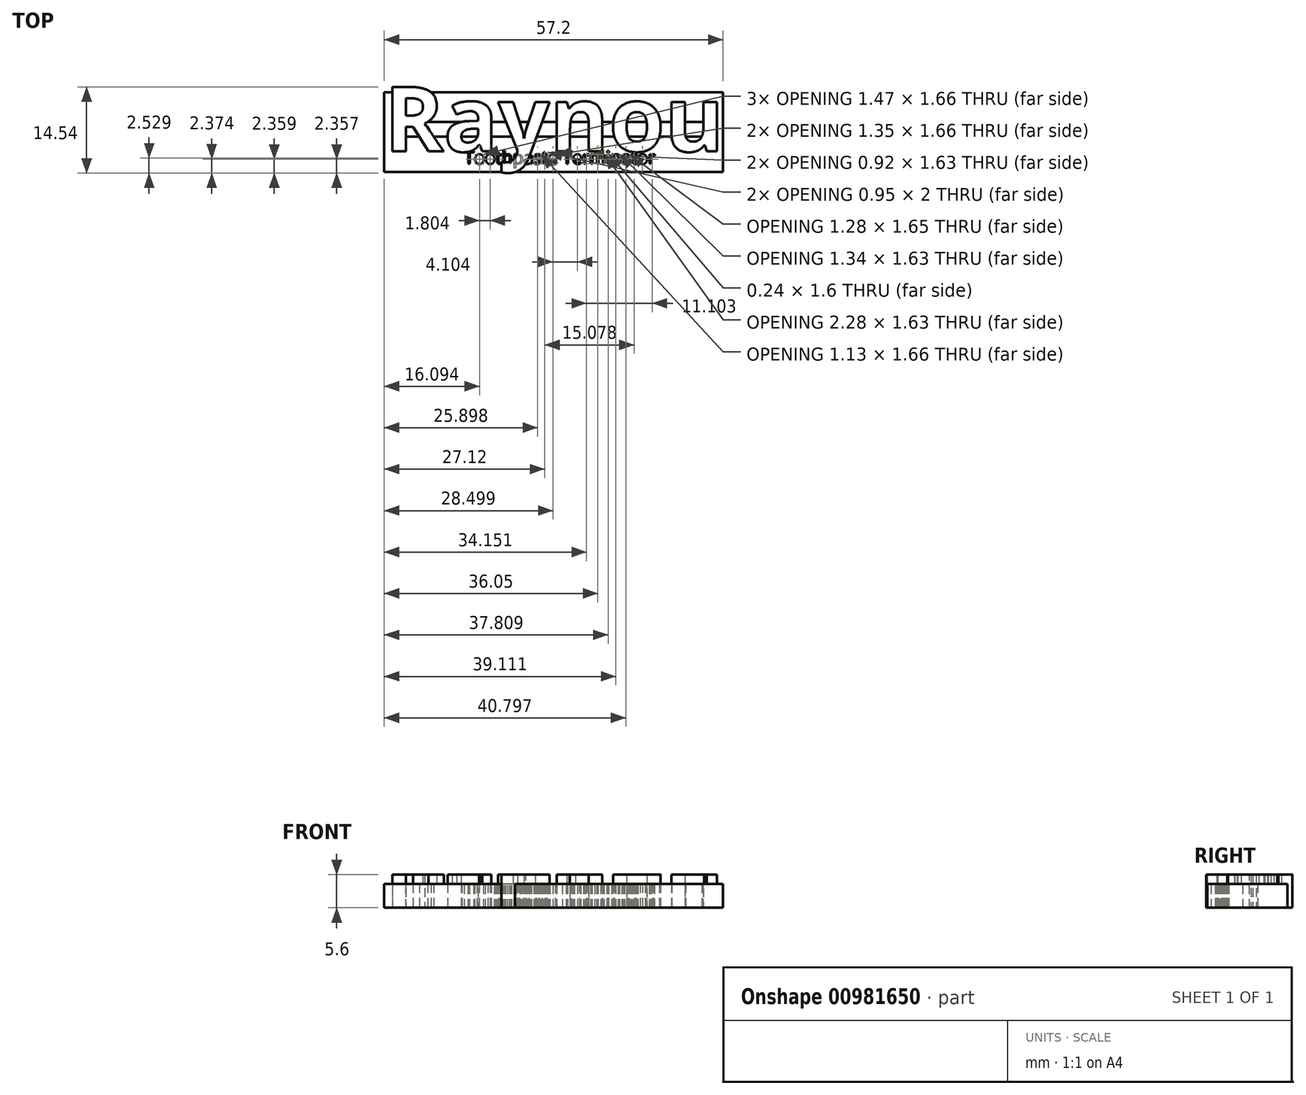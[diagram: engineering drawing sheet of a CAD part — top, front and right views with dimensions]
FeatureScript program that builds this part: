
annotation { "Feature Type Name" : "Feature", "Feature Type Description" : "" }
export const myFeature = defineFeature(function(context is Context, id is Id, definition is map)
    precondition{}
    {
        {
            var Q0;
            Q0=qCreatedBy(makeId("Top.planeOp"),FACE);
            var sketch = newSketch(context, id + "F0", { "sketchPlane" : qUnion([Q0])});
            skLineSegment(sketch, "E0.bottom", {"start": v(-0.37, 8.9) * mm, "end": v(52.83, 8.9) * mm});
            skLineSegment(sketch, "E0.top", {"start": v(-0.37, 6.4) * mm, "end": v(52.83, 6.4) * mm});
            skLineSegment(sketch, "E0.left", {"start": v(-0.37, 8.9) * mm, "end": v(-0.37, 6.4) * mm});
            skLineSegment(sketch, "E0.right", {"start": v(52.83, 8.9) * mm, "end": v(52.83, 6.4) * mm});
            skLineSegment(sketch, "E1.0", {"start": v(-2.37, 13.9) * mm, "end": v(54.83, 13.9) * mm});
            skLineSegment(sketch, "E1.1", {"start": v(-2.37, 13.9) * mm, "end": v(-2.37, 0.4) * mm});
            skLineSegment(sketch, "E1.2", {"start": v(-2.37, 0.4) * mm, "end": v(54.83, 0.4) * mm});
            skLineSegment(sketch, "E1.3", {"start": v(54.83, 13.9) * mm, "end": v(54.83, 0.4) * mm});
            skSolve(sketch);
        }
        {
            var Q0;
            Q0=qCreatedBy(makeId("Top.planeOp"),FACE);
            var sketch = newSketch(context, id + "F1", { "sketchPlane" : qUnion([Q0])});
            skText(sketch, "E2", { "text": "Raynou", "fontName": "OpenSans-Bold.ttf"});
            const initialGuessF1  = {"E2": [-0.00237, 0.0039, 1, 0, 0.01097]};
            skSetInitialGuess(sketch, initialGuessF1);
            skSolve(sketch);
        }
        {
            var Q0;
            Q0=makeQuery(id+"F0.imprint","IMPRINT",FACE,{"disambiguationData":[TD([[makeQuery(id+"F0.imprint","IMPRINT",EDGE,{"derivedFrom":sQuery(id+"F0.wireOp",EDGE,"E0.bottom")}),1.0]])]});
            var Q1;
            Q1=makeQuery(id+"F1.imprint","IMPRINT",FACE,{"disambiguationData":[TD([[makeQuery(id+"F1.imprint","IMPRINT",EDGE,{"derivedFrom":sQuery(id+"F1.wireOp",EDGE,"E2.sketch_text.stroke-19")}),-1.0]])]});
            var Q2;
            Q2=makeQuery(id+"F1.imprint","IMPRINT",FACE,{"disambiguationData":[TD([[makeQuery(id+"F1.imprint","IMPRINT",EDGE,{"derivedFrom":sQuery(id+"F1.wireOp",EDGE,"E2.sketch_text.stroke-0")}),-1.0]])]});
            var Q3;
            Q3=makeQuery(id+"F1.imprint","IMPRINT",FACE,{"disambiguationData":[TD([[makeQuery(id+"F1.imprint","IMPRINT",EDGE,{"derivedFrom":sQuery(id+"F1.wireOp",EDGE,"E2.sketch_text.stroke-44")}),-1.0]])]});
            var Q4;
            Q4=makeQuery(id+"F1.imprint","IMPRINT",FACE,{"disambiguationData":[TD([[makeQuery(id+"F1.imprint","IMPRINT",EDGE,{"derivedFrom":sQuery(id+"F1.wireOp",EDGE,"E2.sketch_text.stroke-61")}),-1.0]])]});
            var Q5;
            Q5=makeQuery(id+"F1.imprint","IMPRINT",FACE,{"disambiguationData":[TD([[makeQuery(id+"F1.imprint","IMPRINT",EDGE,{"derivedFrom":sQuery(id+"F1.wireOp",EDGE,"E2.sketch_text.stroke-78")}),-1.0]])]});
            var Q6;
            Q6=makeQuery(id+"F1.imprint","IMPRINT",FACE,{"disambiguationData":[TD([[makeQuery(id+"F1.imprint","IMPRINT",EDGE,{"derivedFrom":sQuery(id+"F1.wireOp",EDGE,"E2.sketch_text.stroke-96")}),-1.0]])]});
            extrude(context, id + "F2", {"entities" : qUnion([Q0, Q1, Q2, Q3, Q4, Q5, Q6]), "depth" : 4 * mm, "offsetDistance" : 25 * mm});
        }
        {
            var Q0;
            Q0=makeQuery(id+"F2.opExtrude","SWEPT_BODY",BODY,{"disambiguationData":[OSD([sQuery(id+"F1.wireOp",EDGE,"E2.sketch_text.stroke-0"),sQuery(id+"F1.wireOp",EDGE,"E2.sketch_text.stroke-1"),sQuery(id+"F1.wireOp",EDGE,"E2.sketch_text.stroke-2"),sQuery(id+"F1.wireOp",EDGE,"E2.sketch_text.stroke-3"),sQuery(id+"F1.wireOp",EDGE,"E2.sketch_text.stroke-4"),sQuery(id+"F1.wireOp",EDGE,"E2.sketch_text.stroke-5"),sQuery(id+"F1.wireOp",EDGE,"E2.sketch_text.stroke-6"),sQuery(id+"F1.wireOp",EDGE,"E2.sketch_text.stroke-7"),sQuery(id+"F1.wireOp",EDGE,"E2.sketch_text.stroke-8"),sQuery(id+"F1.wireOp",EDGE,"E2.sketch_text.stroke-9"),sQuery(id+"F1.wireOp",EDGE,"E2.sketch_text.stroke-10"),sQuery(id+"F1.wireOp",EDGE,"E2.sketch_text.stroke-11"),sQuery(id+"F1.wireOp",EDGE,"E2.sketch_text.stroke-12"),sQuery(id+"F1.wireOp",EDGE,"E2.sketch_text.stroke-13"),sQuery(id+"F1.wireOp",EDGE,"E2.sketch_text.stroke-14"),sQuery(id+"F1.wireOp",EDGE,"E2.sketch_text.stroke-15"),sQuery(id+"F1.wireOp",EDGE,"E2.sketch_text.stroke-16"),sQuery(id+"F1.wireOp",EDGE,"E2.sketch_text.stroke-17"),sQuery(id+"F1.wireOp",EDGE,"E2.sketch_text.stroke-18")])]});
            var Q1;
            Q1=makeQuery(id+"F2.opExtrude","SWEPT_BODY",BODY,{"disambiguationData":[OSD([sQuery(id+"F0.wireOp",EDGE,"E0.bottom"),sQuery(id+"F0.wireOp",EDGE,"E0.top"),sQuery(id+"F0.wireOp",EDGE,"E0.left"),sQuery(id+"F0.wireOp",EDGE,"E0.right"),sQuery(id+"F0.wireOp",EDGE,"E1.0"),sQuery(id+"F0.wireOp",EDGE,"E1.1"),sQuery(id+"F0.wireOp",EDGE,"E1.2"),sQuery(id+"F0.wireOp",EDGE,"E1.3")])]});
            var Q2;
            Q2=makeQuery(id+"F2.opExtrude","SWEPT_BODY",BODY,{"disambiguationData":[OSD([sQuery(id+"F1.wireOp",EDGE,"E2.sketch_text.stroke-19"),sQuery(id+"F1.wireOp",EDGE,"E2.sketch_text.stroke-20"),sQuery(id+"F1.wireOp",EDGE,"E2.sketch_text.stroke-21"),sQuery(id+"F1.wireOp",EDGE,"E2.sketch_text.stroke-22"),sQuery(id+"F1.wireOp",EDGE,"E2.sketch_text.stroke-23"),sQuery(id+"F1.wireOp",EDGE,"E2.sketch_text.stroke-24"),sQuery(id+"F1.wireOp",EDGE,"E2.sketch_text.stroke-25"),sQuery(id+"F1.wireOp",EDGE,"E2.sketch_text.stroke-26"),sQuery(id+"F1.wireOp",EDGE,"E2.sketch_text.stroke-27"),sQuery(id+"F1.wireOp",EDGE,"E2.sketch_text.stroke-28"),sQuery(id+"F1.wireOp",EDGE,"E2.sketch_text.stroke-29"),sQuery(id+"F1.wireOp",EDGE,"E2.sketch_text.stroke-30"),sQuery(id+"F1.wireOp",EDGE,"E2.sketch_text.stroke-31"),sQuery(id+"F1.wireOp",EDGE,"E2.sketch_text.stroke-32"),sQuery(id+"F1.wireOp",EDGE,"E2.sketch_text.stroke-33"),sQuery(id+"F1.wireOp",EDGE,"E2.sketch_text.stroke-34"),sQuery(id+"F1.wireOp",EDGE,"E2.sketch_text.stroke-35"),sQuery(id+"F1.wireOp",EDGE,"E2.sketch_text.stroke-36"),sQuery(id+"F1.wireOp",EDGE,"E2.sketch_text.stroke-37"),sQuery(id+"F1.wireOp",EDGE,"E2.sketch_text.stroke-38"),sQuery(id+"F1.wireOp",EDGE,"E2.sketch_text.stroke-39"),sQuery(id+"F1.wireOp",EDGE,"E2.sketch_text.stroke-40"),sQuery(id+"F1.wireOp",EDGE,"E2.sketch_text.stroke-41"),sQuery(id+"F1.wireOp",EDGE,"E2.sketch_text.stroke-42"),sQuery(id+"F1.wireOp",EDGE,"E2.sketch_text.stroke-43")])]});
            var Q3;
            Q3=makeQuery(id+"F2.opExtrude","SWEPT_BODY",BODY,{"disambiguationData":[OSD([sQuery(id+"F1.wireOp",EDGE,"E2.sketch_text.stroke-44"),sQuery(id+"F1.wireOp",EDGE,"E2.sketch_text.stroke-45"),sQuery(id+"F1.wireOp",EDGE,"E2.sketch_text.stroke-46"),sQuery(id+"F1.wireOp",EDGE,"E2.sketch_text.stroke-47"),sQuery(id+"F1.wireOp",EDGE,"E2.sketch_text.stroke-48"),sQuery(id+"F1.wireOp",EDGE,"E2.sketch_text.stroke-49"),sQuery(id+"F1.wireOp",EDGE,"E2.sketch_text.stroke-50"),sQuery(id+"F1.wireOp",EDGE,"E2.sketch_text.stroke-51"),sQuery(id+"F1.wireOp",EDGE,"E2.sketch_text.stroke-52"),sQuery(id+"F1.wireOp",EDGE,"E2.sketch_text.stroke-53"),sQuery(id+"F1.wireOp",EDGE,"E2.sketch_text.stroke-54"),sQuery(id+"F1.wireOp",EDGE,"E2.sketch_text.stroke-55"),sQuery(id+"F1.wireOp",EDGE,"E2.sketch_text.stroke-56"),sQuery(id+"F1.wireOp",EDGE,"E2.sketch_text.stroke-57"),sQuery(id+"F1.wireOp",EDGE,"E2.sketch_text.stroke-58"),sQuery(id+"F1.wireOp",EDGE,"E2.sketch_text.stroke-59"),sQuery(id+"F1.wireOp",EDGE,"E2.sketch_text.stroke-60")])]});
            var Q4;
            Q4=makeQuery(id+"F2.opExtrude","SWEPT_BODY",BODY,{"disambiguationData":[OSD([sQuery(id+"F1.wireOp",EDGE,"E2.sketch_text.stroke-61"),sQuery(id+"F1.wireOp",EDGE,"E2.sketch_text.stroke-62"),sQuery(id+"F1.wireOp",EDGE,"E2.sketch_text.stroke-63"),sQuery(id+"F1.wireOp",EDGE,"E2.sketch_text.stroke-64"),sQuery(id+"F1.wireOp",EDGE,"E2.sketch_text.stroke-65"),sQuery(id+"F1.wireOp",EDGE,"E2.sketch_text.stroke-66"),sQuery(id+"F1.wireOp",EDGE,"E2.sketch_text.stroke-67"),sQuery(id+"F1.wireOp",EDGE,"E2.sketch_text.stroke-68"),sQuery(id+"F1.wireOp",EDGE,"E2.sketch_text.stroke-69"),sQuery(id+"F1.wireOp",EDGE,"E2.sketch_text.stroke-70"),sQuery(id+"F1.wireOp",EDGE,"E2.sketch_text.stroke-71"),sQuery(id+"F1.wireOp",EDGE,"E2.sketch_text.stroke-72"),sQuery(id+"F1.wireOp",EDGE,"E2.sketch_text.stroke-73"),sQuery(id+"F1.wireOp",EDGE,"E2.sketch_text.stroke-74"),sQuery(id+"F1.wireOp",EDGE,"E2.sketch_text.stroke-75"),sQuery(id+"F1.wireOp",EDGE,"E2.sketch_text.stroke-76"),sQuery(id+"F1.wireOp",EDGE,"E2.sketch_text.stroke-77")])]});
            var Q5;
            Q5=makeQuery(id+"F2.opExtrude","SWEPT_BODY",BODY,{"disambiguationData":[OSD([sQuery(id+"F1.wireOp",EDGE,"E2.sketch_text.stroke-78"),sQuery(id+"F1.wireOp",EDGE,"E2.sketch_text.stroke-79"),sQuery(id+"F1.wireOp",EDGE,"E2.sketch_text.stroke-80"),sQuery(id+"F1.wireOp",EDGE,"E2.sketch_text.stroke-81"),sQuery(id+"F1.wireOp",EDGE,"E2.sketch_text.stroke-82"),sQuery(id+"F1.wireOp",EDGE,"E2.sketch_text.stroke-83"),sQuery(id+"F1.wireOp",EDGE,"E2.sketch_text.stroke-84"),sQuery(id+"F1.wireOp",EDGE,"E2.sketch_text.stroke-85"),sQuery(id+"F1.wireOp",EDGE,"E2.sketch_text.stroke-86"),sQuery(id+"F1.wireOp",EDGE,"E2.sketch_text.stroke-87"),sQuery(id+"F1.wireOp",EDGE,"E2.sketch_text.stroke-88"),sQuery(id+"F1.wireOp",EDGE,"E2.sketch_text.stroke-89"),sQuery(id+"F1.wireOp",EDGE,"E2.sketch_text.stroke-90"),sQuery(id+"F1.wireOp",EDGE,"E2.sketch_text.stroke-91"),sQuery(id+"F1.wireOp",EDGE,"E2.sketch_text.stroke-92"),sQuery(id+"F1.wireOp",EDGE,"E2.sketch_text.stroke-93"),sQuery(id+"F1.wireOp",EDGE,"E2.sketch_text.stroke-94"),sQuery(id+"F1.wireOp",EDGE,"E2.sketch_text.stroke-95")])]});
            var Q6;
            Q6=makeQuery(id+"F2.opExtrude","SWEPT_BODY",BODY,{"disambiguationData":[OSD([sQuery(id+"F1.wireOp",EDGE,"E2.sketch_text.stroke-96"),sQuery(id+"F1.wireOp",EDGE,"E2.sketch_text.stroke-97"),sQuery(id+"F1.wireOp",EDGE,"E2.sketch_text.stroke-98"),sQuery(id+"F1.wireOp",EDGE,"E2.sketch_text.stroke-99"),sQuery(id+"F1.wireOp",EDGE,"E2.sketch_text.stroke-100"),sQuery(id+"F1.wireOp",EDGE,"E2.sketch_text.stroke-101"),sQuery(id+"F1.wireOp",EDGE,"E2.sketch_text.stroke-102"),sQuery(id+"F1.wireOp",EDGE,"E2.sketch_text.stroke-103"),sQuery(id+"F1.wireOp",EDGE,"E2.sketch_text.stroke-104"),sQuery(id+"F1.wireOp",EDGE,"E2.sketch_text.stroke-105"),sQuery(id+"F1.wireOp",EDGE,"E2.sketch_text.stroke-106"),sQuery(id+"F1.wireOp",EDGE,"E2.sketch_text.stroke-107"),sQuery(id+"F1.wireOp",EDGE,"E2.sketch_text.stroke-108"),sQuery(id+"F1.wireOp",EDGE,"E2.sketch_text.stroke-109"),sQuery(id+"F1.wireOp",EDGE,"E2.sketch_text.stroke-110"),sQuery(id+"F1.wireOp",EDGE,"E2.sketch_text.stroke-111"),sQuery(id+"F1.wireOp",EDGE,"E2.sketch_text.stroke-112")])]});
            booleanBodies(context, id + "F3", {"operationType" : BooleanOperationType.UNION, "tools" : qUnion([Q0, Q1, Q2, Q3, Q4, Q5, Q6])});
        }
        {
            var Q0;
            Q0 = qSketchRegion(id + "F1", true);
            extrude(context, id + "F4", {"entities" : qUnion([Q0]), "operationType" : NewBodyOperationType.ADD, "depth" : 5.6 * mm, "offsetDistance" : 25 * mm});
        }
        {
            var Q0;
            Q0=makeQuery(id+"F3.opBoolean","MERGE",FACE,{"derivedFrom":[makeQuery(id+"F2.opExtrude","CAP_FACE",FACE,{"disambiguationData":[OSD([sQuery(id+"F0.wireOp",EDGE,"E0.bottom"),sQuery(id+"F0.wireOp",EDGE,"E0.top"),sQuery(id+"F0.wireOp",EDGE,"E0.left"),sQuery(id+"F0.wireOp",EDGE,"E0.right"),sQuery(id+"F0.wireOp",EDGE,"E1.0"),sQuery(id+"F0.wireOp",EDGE,"E1.1"),sQuery(id+"F0.wireOp",EDGE,"E1.2"),sQuery(id+"F0.wireOp",EDGE,"E1.3")])],"isStart":false}),makeQuery(id+"F2.opExtrude","CAP_FACE",FACE,{"disambiguationData":[OSD([sQuery(id+"F1.wireOp",EDGE,"E2.sketch_text.stroke-0"),sQuery(id+"F1.wireOp",EDGE,"E2.sketch_text.stroke-1"),sQuery(id+"F1.wireOp",EDGE,"E2.sketch_text.stroke-2"),sQuery(id+"F1.wireOp",EDGE,"E2.sketch_text.stroke-3"),sQuery(id+"F1.wireOp",EDGE,"E2.sketch_text.stroke-4"),sQuery(id+"F1.wireOp",EDGE,"E2.sketch_text.stroke-5"),sQuery(id+"F1.wireOp",EDGE,"E2.sketch_text.stroke-6"),sQuery(id+"F1.wireOp",EDGE,"E2.sketch_text.stroke-7"),sQuery(id+"F1.wireOp",EDGE,"E2.sketch_text.stroke-8"),sQuery(id+"F1.wireOp",EDGE,"E2.sketch_text.stroke-9"),sQuery(id+"F1.wireOp",EDGE,"E2.sketch_text.stroke-10"),sQuery(id+"F1.wireOp",EDGE,"E2.sketch_text.stroke-11"),sQuery(id+"F1.wireOp",EDGE,"E2.sketch_text.stroke-12"),sQuery(id+"F1.wireOp",EDGE,"E2.sketch_text.stroke-13"),sQuery(id+"F1.wireOp",EDGE,"E2.sketch_text.stroke-14"),sQuery(id+"F1.wireOp",EDGE,"E2.sketch_text.stroke-15"),sQuery(id+"F1.wireOp",EDGE,"E2.sketch_text.stroke-16"),sQuery(id+"F1.wireOp",EDGE,"E2.sketch_text.stroke-17"),sQuery(id+"F1.wireOp",EDGE,"E2.sketch_text.stroke-18")])],"isStart":false}),makeQuery(id+"F2.opExtrude","CAP_FACE",FACE,{"disambiguationData":[OSD([sQuery(id+"F1.wireOp",EDGE,"E2.sketch_text.stroke-19"),sQuery(id+"F1.wireOp",EDGE,"E2.sketch_text.stroke-20"),sQuery(id+"F1.wireOp",EDGE,"E2.sketch_text.stroke-21"),sQuery(id+"F1.wireOp",EDGE,"E2.sketch_text.stroke-22"),sQuery(id+"F1.wireOp",EDGE,"E2.sketch_text.stroke-23"),sQuery(id+"F1.wireOp",EDGE,"E2.sketch_text.stroke-24"),sQuery(id+"F1.wireOp",EDGE,"E2.sketch_text.stroke-25"),sQuery(id+"F1.wireOp",EDGE,"E2.sketch_text.stroke-26"),sQuery(id+"F1.wireOp",EDGE,"E2.sketch_text.stroke-27"),sQuery(id+"F1.wireOp",EDGE,"E2.sketch_text.stroke-28"),sQuery(id+"F1.wireOp",EDGE,"E2.sketch_text.stroke-29"),sQuery(id+"F1.wireOp",EDGE,"E2.sketch_text.stroke-30"),sQuery(id+"F1.wireOp",EDGE,"E2.sketch_text.stroke-31"),sQuery(id+"F1.wireOp",EDGE,"E2.sketch_text.stroke-32"),sQuery(id+"F1.wireOp",EDGE,"E2.sketch_text.stroke-33"),sQuery(id+"F1.wireOp",EDGE,"E2.sketch_text.stroke-34"),sQuery(id+"F1.wireOp",EDGE,"E2.sketch_text.stroke-35"),sQuery(id+"F1.wireOp",EDGE,"E2.sketch_text.stroke-36"),sQuery(id+"F1.wireOp",EDGE,"E2.sketch_text.stroke-37"),sQuery(id+"F1.wireOp",EDGE,"E2.sketch_text.stroke-38"),sQuery(id+"F1.wireOp",EDGE,"E2.sketch_text.stroke-39"),sQuery(id+"F1.wireOp",EDGE,"E2.sketch_text.stroke-40"),sQuery(id+"F1.wireOp",EDGE,"E2.sketch_text.stroke-41"),sQuery(id+"F1.wireOp",EDGE,"E2.sketch_text.stroke-42"),sQuery(id+"F1.wireOp",EDGE,"E2.sketch_text.stroke-43")])],"isStart":false}),makeQuery(id+"F2.opExtrude","CAP_FACE",FACE,{"disambiguationData":[OSD([sQuery(id+"F1.wireOp",EDGE,"E2.sketch_text.stroke-44"),sQuery(id+"F1.wireOp",EDGE,"E2.sketch_text.stroke-45"),sQuery(id+"F1.wireOp",EDGE,"E2.sketch_text.stroke-46"),sQuery(id+"F1.wireOp",EDGE,"E2.sketch_text.stroke-47"),sQuery(id+"F1.wireOp",EDGE,"E2.sketch_text.stroke-48"),sQuery(id+"F1.wireOp",EDGE,"E2.sketch_text.stroke-49"),sQuery(id+"F1.wireOp",EDGE,"E2.sketch_text.stroke-50"),sQuery(id+"F1.wireOp",EDGE,"E2.sketch_text.stroke-51"),sQuery(id+"F1.wireOp",EDGE,"E2.sketch_text.stroke-52"),sQuery(id+"F1.wireOp",EDGE,"E2.sketch_text.stroke-53"),sQuery(id+"F1.wireOp",EDGE,"E2.sketch_text.stroke-54"),sQuery(id+"F1.wireOp",EDGE,"E2.sketch_text.stroke-55"),sQuery(id+"F1.wireOp",EDGE,"E2.sketch_text.stroke-56"),sQuery(id+"F1.wireOp",EDGE,"E2.sketch_text.stroke-57"),sQuery(id+"F1.wireOp",EDGE,"E2.sketch_text.stroke-58"),sQuery(id+"F1.wireOp",EDGE,"E2.sketch_text.stroke-59"),sQuery(id+"F1.wireOp",EDGE,"E2.sketch_text.stroke-60")])],"isStart":false}),makeQuery(id+"F2.opExtrude","CAP_FACE",FACE,{"disambiguationData":[OSD([sQuery(id+"F1.wireOp",EDGE,"E2.sketch_text.stroke-61"),sQuery(id+"F1.wireOp",EDGE,"E2.sketch_text.stroke-62"),sQuery(id+"F1.wireOp",EDGE,"E2.sketch_text.stroke-63"),sQuery(id+"F1.wireOp",EDGE,"E2.sketch_text.stroke-64"),sQuery(id+"F1.wireOp",EDGE,"E2.sketch_text.stroke-65"),sQuery(id+"F1.wireOp",EDGE,"E2.sketch_text.stroke-66"),sQuery(id+"F1.wireOp",EDGE,"E2.sketch_text.stroke-67"),sQuery(id+"F1.wireOp",EDGE,"E2.sketch_text.stroke-68"),sQuery(id+"F1.wireOp",EDGE,"E2.sketch_text.stroke-69"),sQuery(id+"F1.wireOp",EDGE,"E2.sketch_text.stroke-70"),sQuery(id+"F1.wireOp",EDGE,"E2.sketch_text.stroke-71"),sQuery(id+"F1.wireOp",EDGE,"E2.sketch_text.stroke-72"),sQuery(id+"F1.wireOp",EDGE,"E2.sketch_text.stroke-73"),sQuery(id+"F1.wireOp",EDGE,"E2.sketch_text.stroke-74"),sQuery(id+"F1.wireOp",EDGE,"E2.sketch_text.stroke-75"),sQuery(id+"F1.wireOp",EDGE,"E2.sketch_text.stroke-76"),sQuery(id+"F1.wireOp",EDGE,"E2.sketch_text.stroke-77")])],"isStart":false}),makeQuery(id+"F2.opExtrude","CAP_FACE",FACE,{"disambiguationData":[OSD([sQuery(id+"F1.wireOp",EDGE,"E2.sketch_text.stroke-78"),sQuery(id+"F1.wireOp",EDGE,"E2.sketch_text.stroke-79"),sQuery(id+"F1.wireOp",EDGE,"E2.sketch_text.stroke-80"),sQuery(id+"F1.wireOp",EDGE,"E2.sketch_text.stroke-81"),sQuery(id+"F1.wireOp",EDGE,"E2.sketch_text.stroke-82"),sQuery(id+"F1.wireOp",EDGE,"E2.sketch_text.stroke-83"),sQuery(id+"F1.wireOp",EDGE,"E2.sketch_text.stroke-84"),sQuery(id+"F1.wireOp",EDGE,"E2.sketch_text.stroke-85"),sQuery(id+"F1.wireOp",EDGE,"E2.sketch_text.stroke-86"),sQuery(id+"F1.wireOp",EDGE,"E2.sketch_text.stroke-87"),sQuery(id+"F1.wireOp",EDGE,"E2.sketch_text.stroke-88"),sQuery(id+"F1.wireOp",EDGE,"E2.sketch_text.stroke-89"),sQuery(id+"F1.wireOp",EDGE,"E2.sketch_text.stroke-90"),sQuery(id+"F1.wireOp",EDGE,"E2.sketch_text.stroke-91"),sQuery(id+"F1.wireOp",EDGE,"E2.sketch_text.stroke-92"),sQuery(id+"F1.wireOp",EDGE,"E2.sketch_text.stroke-93"),sQuery(id+"F1.wireOp",EDGE,"E2.sketch_text.stroke-94"),sQuery(id+"F1.wireOp",EDGE,"E2.sketch_text.stroke-95")])],"isStart":false}),makeQuery(id+"F2.opExtrude","CAP_FACE",FACE,{"disambiguationData":[OSD([sQuery(id+"F1.wireOp",EDGE,"E2.sketch_text.stroke-96"),sQuery(id+"F1.wireOp",EDGE,"E2.sketch_text.stroke-97"),sQuery(id+"F1.wireOp",EDGE,"E2.sketch_text.stroke-98"),sQuery(id+"F1.wireOp",EDGE,"E2.sketch_text.stroke-99"),sQuery(id+"F1.wireOp",EDGE,"E2.sketch_text.stroke-100"),sQuery(id+"F1.wireOp",EDGE,"E2.sketch_text.stroke-101"),sQuery(id+"F1.wireOp",EDGE,"E2.sketch_text.stroke-102"),sQuery(id+"F1.wireOp",EDGE,"E2.sketch_text.stroke-103"),sQuery(id+"F1.wireOp",EDGE,"E2.sketch_text.stroke-104"),sQuery(id+"F1.wireOp",EDGE,"E2.sketch_text.stroke-105"),sQuery(id+"F1.wireOp",EDGE,"E2.sketch_text.stroke-106"),sQuery(id+"F1.wireOp",EDGE,"E2.sketch_text.stroke-107"),sQuery(id+"F1.wireOp",EDGE,"E2.sketch_text.stroke-108"),sQuery(id+"F1.wireOp",EDGE,"E2.sketch_text.stroke-109"),sQuery(id+"F1.wireOp",EDGE,"E2.sketch_text.stroke-110"),sQuery(id+"F1.wireOp",EDGE,"E2.sketch_text.stroke-111"),sQuery(id+"F1.wireOp",EDGE,"E2.sketch_text.stroke-112")])],"isStart":false})]});
            var sketch = newSketch(context, id + "F5", { "sketchPlane" : qUnion([Q0])});
            skText(sketch, "E3", { "text": "Toothpaste Terminator ", "fontName": "OpenSans-Regular.ttf"});
            const initialGuessF5  = {"E3": [0.01117, 0.0018, 1, 0, 0.00215]};
            skSetInitialGuess(sketch, initialGuessF5);
            skSolve(sketch);
        }
        {
            var Q0;
            Q0 = qSketchRegion(id + "F5", true);
            extrude(context, id + "F6", {"entities" : qUnion([Q0]), "operationType" : NewBodyOperationType.REMOVE, "oppositeDirection" : true, "depth" : 25 * mm, "offsetDistance" : 25 * mm});
        }
        {
            var Q0;
            Q0=makeQuery(id+"F6.boolean.opBoolean","SPLIT",FACE,{"disambiguationData":[TD([makeQuery(id+"F6.opExtrude","SWEPT_FACE",FACE,{"disambiguationData":[OSD([sQuery(id+"F5.wireOp",EDGE,"E3.sketch_text.stroke-34")])]})])],"derivedFrom":makeQuery(id+"F3.opBoolean","MERGE",FACE,{"derivedFrom":[makeQuery(id+"F2.opExtrude","CAP_FACE",FACE,{"disambiguationData":[OSD([sQuery(id+"F0.wireOp",EDGE,"E0.bottom"),sQuery(id+"F0.wireOp",EDGE,"E0.top"),sQuery(id+"F0.wireOp",EDGE,"E0.left"),sQuery(id+"F0.wireOp",EDGE,"E0.right"),sQuery(id+"F0.wireOp",EDGE,"E1.0"),sQuery(id+"F0.wireOp",EDGE,"E1.1"),sQuery(id+"F0.wireOp",EDGE,"E1.2"),sQuery(id+"F0.wireOp",EDGE,"E1.3")])],"isStart":false}),makeQuery(id+"F2.opExtrude","CAP_FACE",FACE,{"disambiguationData":[OSD([sQuery(id+"F1.wireOp",EDGE,"E2.sketch_text.stroke-0"),sQuery(id+"F1.wireOp",EDGE,"E2.sketch_text.stroke-1"),sQuery(id+"F1.wireOp",EDGE,"E2.sketch_text.stroke-2"),sQuery(id+"F1.wireOp",EDGE,"E2.sketch_text.stroke-3"),sQuery(id+"F1.wireOp",EDGE,"E2.sketch_text.stroke-4"),sQuery(id+"F1.wireOp",EDGE,"E2.sketch_text.stroke-5"),sQuery(id+"F1.wireOp",EDGE,"E2.sketch_text.stroke-6"),sQuery(id+"F1.wireOp",EDGE,"E2.sketch_text.stroke-7"),sQuery(id+"F1.wireOp",EDGE,"E2.sketch_text.stroke-8"),sQuery(id+"F1.wireOp",EDGE,"E2.sketch_text.stroke-9"),sQuery(id+"F1.wireOp",EDGE,"E2.sketch_text.stroke-10"),sQuery(id+"F1.wireOp",EDGE,"E2.sketch_text.stroke-11"),sQuery(id+"F1.wireOp",EDGE,"E2.sketch_text.stroke-12"),sQuery(id+"F1.wireOp",EDGE,"E2.sketch_text.stroke-13"),sQuery(id+"F1.wireOp",EDGE,"E2.sketch_text.stroke-14"),sQuery(id+"F1.wireOp",EDGE,"E2.sketch_text.stroke-15"),sQuery(id+"F1.wireOp",EDGE,"E2.sketch_text.stroke-16"),sQuery(id+"F1.wireOp",EDGE,"E2.sketch_text.stroke-17"),sQuery(id+"F1.wireOp",EDGE,"E2.sketch_text.stroke-18")])],"isStart":false}),makeQuery(id+"F2.opExtrude","CAP_FACE",FACE,{"disambiguationData":[OSD([sQuery(id+"F1.wireOp",EDGE,"E2.sketch_text.stroke-19"),sQuery(id+"F1.wireOp",EDGE,"E2.sketch_text.stroke-20"),sQuery(id+"F1.wireOp",EDGE,"E2.sketch_text.stroke-21"),sQuery(id+"F1.wireOp",EDGE,"E2.sketch_text.stroke-22"),sQuery(id+"F1.wireOp",EDGE,"E2.sketch_text.stroke-23"),sQuery(id+"F1.wireOp",EDGE,"E2.sketch_text.stroke-24"),sQuery(id+"F1.wireOp",EDGE,"E2.sketch_text.stroke-25"),sQuery(id+"F1.wireOp",EDGE,"E2.sketch_text.stroke-26"),sQuery(id+"F1.wireOp",EDGE,"E2.sketch_text.stroke-27"),sQuery(id+"F1.wireOp",EDGE,"E2.sketch_text.stroke-28"),sQuery(id+"F1.wireOp",EDGE,"E2.sketch_text.stroke-29"),sQuery(id+"F1.wireOp",EDGE,"E2.sketch_text.stroke-30"),sQuery(id+"F1.wireOp",EDGE,"E2.sketch_text.stroke-31"),sQuery(id+"F1.wireOp",EDGE,"E2.sketch_text.stroke-32"),sQuery(id+"F1.wireOp",EDGE,"E2.sketch_text.stroke-33"),sQuery(id+"F1.wireOp",EDGE,"E2.sketch_text.stroke-34"),sQuery(id+"F1.wireOp",EDGE,"E2.sketch_text.stroke-35"),sQuery(id+"F1.wireOp",EDGE,"E2.sketch_text.stroke-36"),sQuery(id+"F1.wireOp",EDGE,"E2.sketch_text.stroke-37"),sQuery(id+"F1.wireOp",EDGE,"E2.sketch_text.stroke-38"),sQuery(id+"F1.wireOp",EDGE,"E2.sketch_text.stroke-39"),sQuery(id+"F1.wireOp",EDGE,"E2.sketch_text.stroke-40"),sQuery(id+"F1.wireOp",EDGE,"E2.sketch_text.stroke-41"),sQuery(id+"F1.wireOp",EDGE,"E2.sketch_text.stroke-42"),sQuery(id+"F1.wireOp",EDGE,"E2.sketch_text.stroke-43")])],"isStart":false}),makeQuery(id+"F2.opExtrude","CAP_FACE",FACE,{"disambiguationData":[OSD([sQuery(id+"F1.wireOp",EDGE,"E2.sketch_text.stroke-44"),sQuery(id+"F1.wireOp",EDGE,"E2.sketch_text.stroke-45"),sQuery(id+"F1.wireOp",EDGE,"E2.sketch_text.stroke-46"),sQuery(id+"F1.wireOp",EDGE,"E2.sketch_text.stroke-47"),sQuery(id+"F1.wireOp",EDGE,"E2.sketch_text.stroke-48"),sQuery(id+"F1.wireOp",EDGE,"E2.sketch_text.stroke-49"),sQuery(id+"F1.wireOp",EDGE,"E2.sketch_text.stroke-50"),sQuery(id+"F1.wireOp",EDGE,"E2.sketch_text.stroke-51"),sQuery(id+"F1.wireOp",EDGE,"E2.sketch_text.stroke-52"),sQuery(id+"F1.wireOp",EDGE,"E2.sketch_text.stroke-53"),sQuery(id+"F1.wireOp",EDGE,"E2.sketch_text.stroke-54"),sQuery(id+"F1.wireOp",EDGE,"E2.sketch_text.stroke-55"),sQuery(id+"F1.wireOp",EDGE,"E2.sketch_text.stroke-56"),sQuery(id+"F1.wireOp",EDGE,"E2.sketch_text.stroke-57"),sQuery(id+"F1.wireOp",EDGE,"E2.sketch_text.stroke-58"),sQuery(id+"F1.wireOp",EDGE,"E2.sketch_text.stroke-59"),sQuery(id+"F1.wireOp",EDGE,"E2.sketch_text.stroke-60")])],"isStart":false}),makeQuery(id+"F2.opExtrude","CAP_FACE",FACE,{"disambiguationData":[OSD([sQuery(id+"F1.wireOp",EDGE,"E2.sketch_text.stroke-61"),sQuery(id+"F1.wireOp",EDGE,"E2.sketch_text.stroke-62"),sQuery(id+"F1.wireOp",EDGE,"E2.sketch_text.stroke-63"),sQuery(id+"F1.wireOp",EDGE,"E2.sketch_text.stroke-64"),sQuery(id+"F1.wireOp",EDGE,"E2.sketch_text.stroke-65"),sQuery(id+"F1.wireOp",EDGE,"E2.sketch_text.stroke-66"),sQuery(id+"F1.wireOp",EDGE,"E2.sketch_text.stroke-67"),sQuery(id+"F1.wireOp",EDGE,"E2.sketch_text.stroke-68"),sQuery(id+"F1.wireOp",EDGE,"E2.sketch_text.stroke-69"),sQuery(id+"F1.wireOp",EDGE,"E2.sketch_text.stroke-70"),sQuery(id+"F1.wireOp",EDGE,"E2.sketch_text.stroke-71"),sQuery(id+"F1.wireOp",EDGE,"E2.sketch_text.stroke-72"),sQuery(id+"F1.wireOp",EDGE,"E2.sketch_text.stroke-73"),sQuery(id+"F1.wireOp",EDGE,"E2.sketch_text.stroke-74"),sQuery(id+"F1.wireOp",EDGE,"E2.sketch_text.stroke-75"),sQuery(id+"F1.wireOp",EDGE,"E2.sketch_text.stroke-76"),sQuery(id+"F1.wireOp",EDGE,"E2.sketch_text.stroke-77")])],"isStart":false}),makeQuery(id+"F2.opExtrude","CAP_FACE",FACE,{"disambiguationData":[OSD([sQuery(id+"F1.wireOp",EDGE,"E2.sketch_text.stroke-78"),sQuery(id+"F1.wireOp",EDGE,"E2.sketch_text.stroke-79"),sQuery(id+"F1.wireOp",EDGE,"E2.sketch_text.stroke-80"),sQuery(id+"F1.wireOp",EDGE,"E2.sketch_text.stroke-81"),sQuery(id+"F1.wireOp",EDGE,"E2.sketch_text.stroke-82"),sQuery(id+"F1.wireOp",EDGE,"E2.sketch_text.stroke-83"),sQuery(id+"F1.wireOp",EDGE,"E2.sketch_text.stroke-84"),sQuery(id+"F1.wireOp",EDGE,"E2.sketch_text.stroke-85"),sQuery(id+"F1.wireOp",EDGE,"E2.sketch_text.stroke-86"),sQuery(id+"F1.wireOp",EDGE,"E2.sketch_text.stroke-87"),sQuery(id+"F1.wireOp",EDGE,"E2.sketch_text.stroke-88"),sQuery(id+"F1.wireOp",EDGE,"E2.sketch_text.stroke-89"),sQuery(id+"F1.wireOp",EDGE,"E2.sketch_text.stroke-90"),sQuery(id+"F1.wireOp",EDGE,"E2.sketch_text.stroke-91"),sQuery(id+"F1.wireOp",EDGE,"E2.sketch_text.stroke-92"),sQuery(id+"F1.wireOp",EDGE,"E2.sketch_text.stroke-93"),sQuery(id+"F1.wireOp",EDGE,"E2.sketch_text.stroke-94"),sQuery(id+"F1.wireOp",EDGE,"E2.sketch_text.stroke-95")])],"isStart":false}),makeQuery(id+"F2.opExtrude","CAP_FACE",FACE,{"disambiguationData":[OSD([sQuery(id+"F1.wireOp",EDGE,"E2.sketch_text.stroke-96"),sQuery(id+"F1.wireOp",EDGE,"E2.sketch_text.stroke-97"),sQuery(id+"F1.wireOp",EDGE,"E2.sketch_text.stroke-98"),sQuery(id+"F1.wireOp",EDGE,"E2.sketch_text.stroke-99"),sQuery(id+"F1.wireOp",EDGE,"E2.sketch_text.stroke-100"),sQuery(id+"F1.wireOp",EDGE,"E2.sketch_text.stroke-101"),sQuery(id+"F1.wireOp",EDGE,"E2.sketch_text.stroke-102"),sQuery(id+"F1.wireOp",EDGE,"E2.sketch_text.stroke-103"),sQuery(id+"F1.wireOp",EDGE,"E2.sketch_text.stroke-104"),sQuery(id+"F1.wireOp",EDGE,"E2.sketch_text.stroke-105"),sQuery(id+"F1.wireOp",EDGE,"E2.sketch_text.stroke-106"),sQuery(id+"F1.wireOp",EDGE,"E2.sketch_text.stroke-107"),sQuery(id+"F1.wireOp",EDGE,"E2.sketch_text.stroke-108"),sQuery(id+"F1.wireOp",EDGE,"E2.sketch_text.stroke-109"),sQuery(id+"F1.wireOp",EDGE,"E2.sketch_text.stroke-110"),sQuery(id+"F1.wireOp",EDGE,"E2.sketch_text.stroke-111"),sQuery(id+"F1.wireOp",EDGE,"E2.sketch_text.stroke-112")])],"isStart":false})]})});
            var Q1;
            Q1=makeQuery(id+"F6.boolean.opBoolean","SPLIT",FACE,{"disambiguationData":[TD([makeQuery(id+"F6.opExtrude","SWEPT_FACE",FACE,{"disambiguationData":[OSD([sQuery(id+"F5.wireOp",EDGE,"E3.sketch_text.stroke-95")])]})])],"derivedFrom":makeQuery(id+"F3.opBoolean","MERGE",FACE,{"derivedFrom":[makeQuery(id+"F2.opExtrude","CAP_FACE",FACE,{"disambiguationData":[OSD([sQuery(id+"F0.wireOp",EDGE,"E0.bottom"),sQuery(id+"F0.wireOp",EDGE,"E0.top"),sQuery(id+"F0.wireOp",EDGE,"E0.left"),sQuery(id+"F0.wireOp",EDGE,"E0.right"),sQuery(id+"F0.wireOp",EDGE,"E1.0"),sQuery(id+"F0.wireOp",EDGE,"E1.1"),sQuery(id+"F0.wireOp",EDGE,"E1.2"),sQuery(id+"F0.wireOp",EDGE,"E1.3")])],"isStart":false}),makeQuery(id+"F2.opExtrude","CAP_FACE",FACE,{"disambiguationData":[OSD([sQuery(id+"F1.wireOp",EDGE,"E2.sketch_text.stroke-0"),sQuery(id+"F1.wireOp",EDGE,"E2.sketch_text.stroke-1"),sQuery(id+"F1.wireOp",EDGE,"E2.sketch_text.stroke-2"),sQuery(id+"F1.wireOp",EDGE,"E2.sketch_text.stroke-3"),sQuery(id+"F1.wireOp",EDGE,"E2.sketch_text.stroke-4"),sQuery(id+"F1.wireOp",EDGE,"E2.sketch_text.stroke-5"),sQuery(id+"F1.wireOp",EDGE,"E2.sketch_text.stroke-6"),sQuery(id+"F1.wireOp",EDGE,"E2.sketch_text.stroke-7"),sQuery(id+"F1.wireOp",EDGE,"E2.sketch_text.stroke-8"),sQuery(id+"F1.wireOp",EDGE,"E2.sketch_text.stroke-9"),sQuery(id+"F1.wireOp",EDGE,"E2.sketch_text.stroke-10"),sQuery(id+"F1.wireOp",EDGE,"E2.sketch_text.stroke-11"),sQuery(id+"F1.wireOp",EDGE,"E2.sketch_text.stroke-12"),sQuery(id+"F1.wireOp",EDGE,"E2.sketch_text.stroke-13"),sQuery(id+"F1.wireOp",EDGE,"E2.sketch_text.stroke-14"),sQuery(id+"F1.wireOp",EDGE,"E2.sketch_text.stroke-15"),sQuery(id+"F1.wireOp",EDGE,"E2.sketch_text.stroke-16"),sQuery(id+"F1.wireOp",EDGE,"E2.sketch_text.stroke-17"),sQuery(id+"F1.wireOp",EDGE,"E2.sketch_text.stroke-18")])],"isStart":false}),makeQuery(id+"F2.opExtrude","CAP_FACE",FACE,{"disambiguationData":[OSD([sQuery(id+"F1.wireOp",EDGE,"E2.sketch_text.stroke-19"),sQuery(id+"F1.wireOp",EDGE,"E2.sketch_text.stroke-20"),sQuery(id+"F1.wireOp",EDGE,"E2.sketch_text.stroke-21"),sQuery(id+"F1.wireOp",EDGE,"E2.sketch_text.stroke-22"),sQuery(id+"F1.wireOp",EDGE,"E2.sketch_text.stroke-23"),sQuery(id+"F1.wireOp",EDGE,"E2.sketch_text.stroke-24"),sQuery(id+"F1.wireOp",EDGE,"E2.sketch_text.stroke-25"),sQuery(id+"F1.wireOp",EDGE,"E2.sketch_text.stroke-26"),sQuery(id+"F1.wireOp",EDGE,"E2.sketch_text.stroke-27"),sQuery(id+"F1.wireOp",EDGE,"E2.sketch_text.stroke-28"),sQuery(id+"F1.wireOp",EDGE,"E2.sketch_text.stroke-29"),sQuery(id+"F1.wireOp",EDGE,"E2.sketch_text.stroke-30"),sQuery(id+"F1.wireOp",EDGE,"E2.sketch_text.stroke-31"),sQuery(id+"F1.wireOp",EDGE,"E2.sketch_text.stroke-32"),sQuery(id+"F1.wireOp",EDGE,"E2.sketch_text.stroke-33"),sQuery(id+"F1.wireOp",EDGE,"E2.sketch_text.stroke-34"),sQuery(id+"F1.wireOp",EDGE,"E2.sketch_text.stroke-35"),sQuery(id+"F1.wireOp",EDGE,"E2.sketch_text.stroke-36"),sQuery(id+"F1.wireOp",EDGE,"E2.sketch_text.stroke-37"),sQuery(id+"F1.wireOp",EDGE,"E2.sketch_text.stroke-38"),sQuery(id+"F1.wireOp",EDGE,"E2.sketch_text.stroke-39"),sQuery(id+"F1.wireOp",EDGE,"E2.sketch_text.stroke-40"),sQuery(id+"F1.wireOp",EDGE,"E2.sketch_text.stroke-41"),sQuery(id+"F1.wireOp",EDGE,"E2.sketch_text.stroke-42"),sQuery(id+"F1.wireOp",EDGE,"E2.sketch_text.stroke-43")])],"isStart":false}),makeQuery(id+"F2.opExtrude","CAP_FACE",FACE,{"disambiguationData":[OSD([sQuery(id+"F1.wireOp",EDGE,"E2.sketch_text.stroke-44"),sQuery(id+"F1.wireOp",EDGE,"E2.sketch_text.stroke-45"),sQuery(id+"F1.wireOp",EDGE,"E2.sketch_text.stroke-46"),sQuery(id+"F1.wireOp",EDGE,"E2.sketch_text.stroke-47"),sQuery(id+"F1.wireOp",EDGE,"E2.sketch_text.stroke-48"),sQuery(id+"F1.wireOp",EDGE,"E2.sketch_text.stroke-49"),sQuery(id+"F1.wireOp",EDGE,"E2.sketch_text.stroke-50"),sQuery(id+"F1.wireOp",EDGE,"E2.sketch_text.stroke-51"),sQuery(id+"F1.wireOp",EDGE,"E2.sketch_text.stroke-52"),sQuery(id+"F1.wireOp",EDGE,"E2.sketch_text.stroke-53"),sQuery(id+"F1.wireOp",EDGE,"E2.sketch_text.stroke-54"),sQuery(id+"F1.wireOp",EDGE,"E2.sketch_text.stroke-55"),sQuery(id+"F1.wireOp",EDGE,"E2.sketch_text.stroke-56"),sQuery(id+"F1.wireOp",EDGE,"E2.sketch_text.stroke-57"),sQuery(id+"F1.wireOp",EDGE,"E2.sketch_text.stroke-58"),sQuery(id+"F1.wireOp",EDGE,"E2.sketch_text.stroke-59"),sQuery(id+"F1.wireOp",EDGE,"E2.sketch_text.stroke-60")])],"isStart":false}),makeQuery(id+"F2.opExtrude","CAP_FACE",FACE,{"disambiguationData":[OSD([sQuery(id+"F1.wireOp",EDGE,"E2.sketch_text.stroke-61"),sQuery(id+"F1.wireOp",EDGE,"E2.sketch_text.stroke-62"),sQuery(id+"F1.wireOp",EDGE,"E2.sketch_text.stroke-63"),sQuery(id+"F1.wireOp",EDGE,"E2.sketch_text.stroke-64"),sQuery(id+"F1.wireOp",EDGE,"E2.sketch_text.stroke-65"),sQuery(id+"F1.wireOp",EDGE,"E2.sketch_text.stroke-66"),sQuery(id+"F1.wireOp",EDGE,"E2.sketch_text.stroke-67"),sQuery(id+"F1.wireOp",EDGE,"E2.sketch_text.stroke-68"),sQuery(id+"F1.wireOp",EDGE,"E2.sketch_text.stroke-69"),sQuery(id+"F1.wireOp",EDGE,"E2.sketch_text.stroke-70"),sQuery(id+"F1.wireOp",EDGE,"E2.sketch_text.stroke-71"),sQuery(id+"F1.wireOp",EDGE,"E2.sketch_text.stroke-72"),sQuery(id+"F1.wireOp",EDGE,"E2.sketch_text.stroke-73"),sQuery(id+"F1.wireOp",EDGE,"E2.sketch_text.stroke-74"),sQuery(id+"F1.wireOp",EDGE,"E2.sketch_text.stroke-75"),sQuery(id+"F1.wireOp",EDGE,"E2.sketch_text.stroke-76"),sQuery(id+"F1.wireOp",EDGE,"E2.sketch_text.stroke-77")])],"isStart":false}),makeQuery(id+"F2.opExtrude","CAP_FACE",FACE,{"disambiguationData":[OSD([sQuery(id+"F1.wireOp",EDGE,"E2.sketch_text.stroke-78"),sQuery(id+"F1.wireOp",EDGE,"E2.sketch_text.stroke-79"),sQuery(id+"F1.wireOp",EDGE,"E2.sketch_text.stroke-80"),sQuery(id+"F1.wireOp",EDGE,"E2.sketch_text.stroke-81"),sQuery(id+"F1.wireOp",EDGE,"E2.sketch_text.stroke-82"),sQuery(id+"F1.wireOp",EDGE,"E2.sketch_text.stroke-83"),sQuery(id+"F1.wireOp",EDGE,"E2.sketch_text.stroke-84"),sQuery(id+"F1.wireOp",EDGE,"E2.sketch_text.stroke-85"),sQuery(id+"F1.wireOp",EDGE,"E2.sketch_text.stroke-86"),sQuery(id+"F1.wireOp",EDGE,"E2.sketch_text.stroke-87"),sQuery(id+"F1.wireOp",EDGE,"E2.sketch_text.stroke-88"),sQuery(id+"F1.wireOp",EDGE,"E2.sketch_text.stroke-89"),sQuery(id+"F1.wireOp",EDGE,"E2.sketch_text.stroke-90"),sQuery(id+"F1.wireOp",EDGE,"E2.sketch_text.stroke-91"),sQuery(id+"F1.wireOp",EDGE,"E2.sketch_text.stroke-92"),sQuery(id+"F1.wireOp",EDGE,"E2.sketch_text.stroke-93"),sQuery(id+"F1.wireOp",EDGE,"E2.sketch_text.stroke-94"),sQuery(id+"F1.wireOp",EDGE,"E2.sketch_text.stroke-95")])],"isStart":false}),makeQuery(id+"F2.opExtrude","CAP_FACE",FACE,{"disambiguationData":[OSD([sQuery(id+"F1.wireOp",EDGE,"E2.sketch_text.stroke-96"),sQuery(id+"F1.wireOp",EDGE,"E2.sketch_text.stroke-97"),sQuery(id+"F1.wireOp",EDGE,"E2.sketch_text.stroke-98"),sQuery(id+"F1.wireOp",EDGE,"E2.sketch_text.stroke-99"),sQuery(id+"F1.wireOp",EDGE,"E2.sketch_text.stroke-100"),sQuery(id+"F1.wireOp",EDGE,"E2.sketch_text.stroke-101"),sQuery(id+"F1.wireOp",EDGE,"E2.sketch_text.stroke-102"),sQuery(id+"F1.wireOp",EDGE,"E2.sketch_text.stroke-103"),sQuery(id+"F1.wireOp",EDGE,"E2.sketch_text.stroke-104"),sQuery(id+"F1.wireOp",EDGE,"E2.sketch_text.stroke-105"),sQuery(id+"F1.wireOp",EDGE,"E2.sketch_text.stroke-106"),sQuery(id+"F1.wireOp",EDGE,"E2.sketch_text.stroke-107"),sQuery(id+"F1.wireOp",EDGE,"E2.sketch_text.stroke-108"),sQuery(id+"F1.wireOp",EDGE,"E2.sketch_text.stroke-109"),sQuery(id+"F1.wireOp",EDGE,"E2.sketch_text.stroke-110"),sQuery(id+"F1.wireOp",EDGE,"E2.sketch_text.stroke-111"),sQuery(id+"F1.wireOp",EDGE,"E2.sketch_text.stroke-112")])],"isStart":false})]})});
            var Q2;
            Q2=makeQuery(id+"F6.boolean.opBoolean","SPLIT",FACE,{"disambiguationData":[TD([makeQuery(id+"F6.opExtrude","SWEPT_FACE",FACE,{"disambiguationData":[OSD([sQuery(id+"F5.wireOp",EDGE,"E3.sketch_text.stroke-123")])]})])],"derivedFrom":makeQuery(id+"F3.opBoolean","MERGE",FACE,{"derivedFrom":[makeQuery(id+"F2.opExtrude","CAP_FACE",FACE,{"disambiguationData":[OSD([sQuery(id+"F0.wireOp",EDGE,"E0.bottom"),sQuery(id+"F0.wireOp",EDGE,"E0.top"),sQuery(id+"F0.wireOp",EDGE,"E0.left"),sQuery(id+"F0.wireOp",EDGE,"E0.right"),sQuery(id+"F0.wireOp",EDGE,"E1.0"),sQuery(id+"F0.wireOp",EDGE,"E1.1"),sQuery(id+"F0.wireOp",EDGE,"E1.2"),sQuery(id+"F0.wireOp",EDGE,"E1.3")])],"isStart":false}),makeQuery(id+"F2.opExtrude","CAP_FACE",FACE,{"disambiguationData":[OSD([sQuery(id+"F1.wireOp",EDGE,"E2.sketch_text.stroke-0"),sQuery(id+"F1.wireOp",EDGE,"E2.sketch_text.stroke-1"),sQuery(id+"F1.wireOp",EDGE,"E2.sketch_text.stroke-2"),sQuery(id+"F1.wireOp",EDGE,"E2.sketch_text.stroke-3"),sQuery(id+"F1.wireOp",EDGE,"E2.sketch_text.stroke-4"),sQuery(id+"F1.wireOp",EDGE,"E2.sketch_text.stroke-5"),sQuery(id+"F1.wireOp",EDGE,"E2.sketch_text.stroke-6"),sQuery(id+"F1.wireOp",EDGE,"E2.sketch_text.stroke-7"),sQuery(id+"F1.wireOp",EDGE,"E2.sketch_text.stroke-8"),sQuery(id+"F1.wireOp",EDGE,"E2.sketch_text.stroke-9"),sQuery(id+"F1.wireOp",EDGE,"E2.sketch_text.stroke-10"),sQuery(id+"F1.wireOp",EDGE,"E2.sketch_text.stroke-11"),sQuery(id+"F1.wireOp",EDGE,"E2.sketch_text.stroke-12"),sQuery(id+"F1.wireOp",EDGE,"E2.sketch_text.stroke-13"),sQuery(id+"F1.wireOp",EDGE,"E2.sketch_text.stroke-14"),sQuery(id+"F1.wireOp",EDGE,"E2.sketch_text.stroke-15"),sQuery(id+"F1.wireOp",EDGE,"E2.sketch_text.stroke-16"),sQuery(id+"F1.wireOp",EDGE,"E2.sketch_text.stroke-17"),sQuery(id+"F1.wireOp",EDGE,"E2.sketch_text.stroke-18")])],"isStart":false}),makeQuery(id+"F2.opExtrude","CAP_FACE",FACE,{"disambiguationData":[OSD([sQuery(id+"F1.wireOp",EDGE,"E2.sketch_text.stroke-19"),sQuery(id+"F1.wireOp",EDGE,"E2.sketch_text.stroke-20"),sQuery(id+"F1.wireOp",EDGE,"E2.sketch_text.stroke-21"),sQuery(id+"F1.wireOp",EDGE,"E2.sketch_text.stroke-22"),sQuery(id+"F1.wireOp",EDGE,"E2.sketch_text.stroke-23"),sQuery(id+"F1.wireOp",EDGE,"E2.sketch_text.stroke-24"),sQuery(id+"F1.wireOp",EDGE,"E2.sketch_text.stroke-25"),sQuery(id+"F1.wireOp",EDGE,"E2.sketch_text.stroke-26"),sQuery(id+"F1.wireOp",EDGE,"E2.sketch_text.stroke-27"),sQuery(id+"F1.wireOp",EDGE,"E2.sketch_text.stroke-28"),sQuery(id+"F1.wireOp",EDGE,"E2.sketch_text.stroke-29"),sQuery(id+"F1.wireOp",EDGE,"E2.sketch_text.stroke-30"),sQuery(id+"F1.wireOp",EDGE,"E2.sketch_text.stroke-31"),sQuery(id+"F1.wireOp",EDGE,"E2.sketch_text.stroke-32"),sQuery(id+"F1.wireOp",EDGE,"E2.sketch_text.stroke-33"),sQuery(id+"F1.wireOp",EDGE,"E2.sketch_text.stroke-34"),sQuery(id+"F1.wireOp",EDGE,"E2.sketch_text.stroke-35"),sQuery(id+"F1.wireOp",EDGE,"E2.sketch_text.stroke-36"),sQuery(id+"F1.wireOp",EDGE,"E2.sketch_text.stroke-37"),sQuery(id+"F1.wireOp",EDGE,"E2.sketch_text.stroke-38"),sQuery(id+"F1.wireOp",EDGE,"E2.sketch_text.stroke-39"),sQuery(id+"F1.wireOp",EDGE,"E2.sketch_text.stroke-40"),sQuery(id+"F1.wireOp",EDGE,"E2.sketch_text.stroke-41"),sQuery(id+"F1.wireOp",EDGE,"E2.sketch_text.stroke-42"),sQuery(id+"F1.wireOp",EDGE,"E2.sketch_text.stroke-43")])],"isStart":false}),makeQuery(id+"F2.opExtrude","CAP_FACE",FACE,{"disambiguationData":[OSD([sQuery(id+"F1.wireOp",EDGE,"E2.sketch_text.stroke-44"),sQuery(id+"F1.wireOp",EDGE,"E2.sketch_text.stroke-45"),sQuery(id+"F1.wireOp",EDGE,"E2.sketch_text.stroke-46"),sQuery(id+"F1.wireOp",EDGE,"E2.sketch_text.stroke-47"),sQuery(id+"F1.wireOp",EDGE,"E2.sketch_text.stroke-48"),sQuery(id+"F1.wireOp",EDGE,"E2.sketch_text.stroke-49"),sQuery(id+"F1.wireOp",EDGE,"E2.sketch_text.stroke-50"),sQuery(id+"F1.wireOp",EDGE,"E2.sketch_text.stroke-51"),sQuery(id+"F1.wireOp",EDGE,"E2.sketch_text.stroke-52"),sQuery(id+"F1.wireOp",EDGE,"E2.sketch_text.stroke-53"),sQuery(id+"F1.wireOp",EDGE,"E2.sketch_text.stroke-54"),sQuery(id+"F1.wireOp",EDGE,"E2.sketch_text.stroke-55"),sQuery(id+"F1.wireOp",EDGE,"E2.sketch_text.stroke-56"),sQuery(id+"F1.wireOp",EDGE,"E2.sketch_text.stroke-57"),sQuery(id+"F1.wireOp",EDGE,"E2.sketch_text.stroke-58"),sQuery(id+"F1.wireOp",EDGE,"E2.sketch_text.stroke-59"),sQuery(id+"F1.wireOp",EDGE,"E2.sketch_text.stroke-60")])],"isStart":false}),makeQuery(id+"F2.opExtrude","CAP_FACE",FACE,{"disambiguationData":[OSD([sQuery(id+"F1.wireOp",EDGE,"E2.sketch_text.stroke-61"),sQuery(id+"F1.wireOp",EDGE,"E2.sketch_text.stroke-62"),sQuery(id+"F1.wireOp",EDGE,"E2.sketch_text.stroke-63"),sQuery(id+"F1.wireOp",EDGE,"E2.sketch_text.stroke-64"),sQuery(id+"F1.wireOp",EDGE,"E2.sketch_text.stroke-65"),sQuery(id+"F1.wireOp",EDGE,"E2.sketch_text.stroke-66"),sQuery(id+"F1.wireOp",EDGE,"E2.sketch_text.stroke-67"),sQuery(id+"F1.wireOp",EDGE,"E2.sketch_text.stroke-68"),sQuery(id+"F1.wireOp",EDGE,"E2.sketch_text.stroke-69"),sQuery(id+"F1.wireOp",EDGE,"E2.sketch_text.stroke-70"),sQuery(id+"F1.wireOp",EDGE,"E2.sketch_text.stroke-71"),sQuery(id+"F1.wireOp",EDGE,"E2.sketch_text.stroke-72"),sQuery(id+"F1.wireOp",EDGE,"E2.sketch_text.stroke-73"),sQuery(id+"F1.wireOp",EDGE,"E2.sketch_text.stroke-74"),sQuery(id+"F1.wireOp",EDGE,"E2.sketch_text.stroke-75"),sQuery(id+"F1.wireOp",EDGE,"E2.sketch_text.stroke-76"),sQuery(id+"F1.wireOp",EDGE,"E2.sketch_text.stroke-77")])],"isStart":false}),makeQuery(id+"F2.opExtrude","CAP_FACE",FACE,{"disambiguationData":[OSD([sQuery(id+"F1.wireOp",EDGE,"E2.sketch_text.stroke-78"),sQuery(id+"F1.wireOp",EDGE,"E2.sketch_text.stroke-79"),sQuery(id+"F1.wireOp",EDGE,"E2.sketch_text.stroke-80"),sQuery(id+"F1.wireOp",EDGE,"E2.sketch_text.stroke-81"),sQuery(id+"F1.wireOp",EDGE,"E2.sketch_text.stroke-82"),sQuery(id+"F1.wireOp",EDGE,"E2.sketch_text.stroke-83"),sQuery(id+"F1.wireOp",EDGE,"E2.sketch_text.stroke-84"),sQuery(id+"F1.wireOp",EDGE,"E2.sketch_text.stroke-85"),sQuery(id+"F1.wireOp",EDGE,"E2.sketch_text.stroke-86"),sQuery(id+"F1.wireOp",EDGE,"E2.sketch_text.stroke-87"),sQuery(id+"F1.wireOp",EDGE,"E2.sketch_text.stroke-88"),sQuery(id+"F1.wireOp",EDGE,"E2.sketch_text.stroke-89"),sQuery(id+"F1.wireOp",EDGE,"E2.sketch_text.stroke-90"),sQuery(id+"F1.wireOp",EDGE,"E2.sketch_text.stroke-91"),sQuery(id+"F1.wireOp",EDGE,"E2.sketch_text.stroke-92"),sQuery(id+"F1.wireOp",EDGE,"E2.sketch_text.stroke-93"),sQuery(id+"F1.wireOp",EDGE,"E2.sketch_text.stroke-94"),sQuery(id+"F1.wireOp",EDGE,"E2.sketch_text.stroke-95")])],"isStart":false}),makeQuery(id+"F2.opExtrude","CAP_FACE",FACE,{"disambiguationData":[OSD([sQuery(id+"F1.wireOp",EDGE,"E2.sketch_text.stroke-96"),sQuery(id+"F1.wireOp",EDGE,"E2.sketch_text.stroke-97"),sQuery(id+"F1.wireOp",EDGE,"E2.sketch_text.stroke-98"),sQuery(id+"F1.wireOp",EDGE,"E2.sketch_text.stroke-99"),sQuery(id+"F1.wireOp",EDGE,"E2.sketch_text.stroke-100"),sQuery(id+"F1.wireOp",EDGE,"E2.sketch_text.stroke-101"),sQuery(id+"F1.wireOp",EDGE,"E2.sketch_text.stroke-102"),sQuery(id+"F1.wireOp",EDGE,"E2.sketch_text.stroke-103"),sQuery(id+"F1.wireOp",EDGE,"E2.sketch_text.stroke-104"),sQuery(id+"F1.wireOp",EDGE,"E2.sketch_text.stroke-105"),sQuery(id+"F1.wireOp",EDGE,"E2.sketch_text.stroke-106"),sQuery(id+"F1.wireOp",EDGE,"E2.sketch_text.stroke-107"),sQuery(id+"F1.wireOp",EDGE,"E2.sketch_text.stroke-108"),sQuery(id+"F1.wireOp",EDGE,"E2.sketch_text.stroke-109"),sQuery(id+"F1.wireOp",EDGE,"E2.sketch_text.stroke-110"),sQuery(id+"F1.wireOp",EDGE,"E2.sketch_text.stroke-111"),sQuery(id+"F1.wireOp",EDGE,"E2.sketch_text.stroke-112")])],"isStart":false})]})});
            var Q3;
            Q3=makeQuery(id+"F6.boolean.opBoolean","SPLIT",FACE,{"disambiguationData":[TD([makeQuery(id+"F6.opExtrude","SWEPT_FACE",FACE,{"disambiguationData":[OSD([sQuery(id+"F5.wireOp",EDGE,"E3.sketch_text.stroke-189")])]})])],"derivedFrom":makeQuery(id+"F3.opBoolean","MERGE",FACE,{"derivedFrom":[makeQuery(id+"F2.opExtrude","CAP_FACE",FACE,{"disambiguationData":[OSD([sQuery(id+"F0.wireOp",EDGE,"E0.bottom"),sQuery(id+"F0.wireOp",EDGE,"E0.top"),sQuery(id+"F0.wireOp",EDGE,"E0.left"),sQuery(id+"F0.wireOp",EDGE,"E0.right"),sQuery(id+"F0.wireOp",EDGE,"E1.0"),sQuery(id+"F0.wireOp",EDGE,"E1.1"),sQuery(id+"F0.wireOp",EDGE,"E1.2"),sQuery(id+"F0.wireOp",EDGE,"E1.3")])],"isStart":false}),makeQuery(id+"F2.opExtrude","CAP_FACE",FACE,{"disambiguationData":[OSD([sQuery(id+"F1.wireOp",EDGE,"E2.sketch_text.stroke-0"),sQuery(id+"F1.wireOp",EDGE,"E2.sketch_text.stroke-1"),sQuery(id+"F1.wireOp",EDGE,"E2.sketch_text.stroke-2"),sQuery(id+"F1.wireOp",EDGE,"E2.sketch_text.stroke-3"),sQuery(id+"F1.wireOp",EDGE,"E2.sketch_text.stroke-4"),sQuery(id+"F1.wireOp",EDGE,"E2.sketch_text.stroke-5"),sQuery(id+"F1.wireOp",EDGE,"E2.sketch_text.stroke-6"),sQuery(id+"F1.wireOp",EDGE,"E2.sketch_text.stroke-7"),sQuery(id+"F1.wireOp",EDGE,"E2.sketch_text.stroke-8"),sQuery(id+"F1.wireOp",EDGE,"E2.sketch_text.stroke-9"),sQuery(id+"F1.wireOp",EDGE,"E2.sketch_text.stroke-10"),sQuery(id+"F1.wireOp",EDGE,"E2.sketch_text.stroke-11"),sQuery(id+"F1.wireOp",EDGE,"E2.sketch_text.stroke-12"),sQuery(id+"F1.wireOp",EDGE,"E2.sketch_text.stroke-13"),sQuery(id+"F1.wireOp",EDGE,"E2.sketch_text.stroke-14"),sQuery(id+"F1.wireOp",EDGE,"E2.sketch_text.stroke-15"),sQuery(id+"F1.wireOp",EDGE,"E2.sketch_text.stroke-16"),sQuery(id+"F1.wireOp",EDGE,"E2.sketch_text.stroke-17"),sQuery(id+"F1.wireOp",EDGE,"E2.sketch_text.stroke-18")])],"isStart":false}),makeQuery(id+"F2.opExtrude","CAP_FACE",FACE,{"disambiguationData":[OSD([sQuery(id+"F1.wireOp",EDGE,"E2.sketch_text.stroke-19"),sQuery(id+"F1.wireOp",EDGE,"E2.sketch_text.stroke-20"),sQuery(id+"F1.wireOp",EDGE,"E2.sketch_text.stroke-21"),sQuery(id+"F1.wireOp",EDGE,"E2.sketch_text.stroke-22"),sQuery(id+"F1.wireOp",EDGE,"E2.sketch_text.stroke-23"),sQuery(id+"F1.wireOp",EDGE,"E2.sketch_text.stroke-24"),sQuery(id+"F1.wireOp",EDGE,"E2.sketch_text.stroke-25"),sQuery(id+"F1.wireOp",EDGE,"E2.sketch_text.stroke-26"),sQuery(id+"F1.wireOp",EDGE,"E2.sketch_text.stroke-27"),sQuery(id+"F1.wireOp",EDGE,"E2.sketch_text.stroke-28"),sQuery(id+"F1.wireOp",EDGE,"E2.sketch_text.stroke-29"),sQuery(id+"F1.wireOp",EDGE,"E2.sketch_text.stroke-30"),sQuery(id+"F1.wireOp",EDGE,"E2.sketch_text.stroke-31"),sQuery(id+"F1.wireOp",EDGE,"E2.sketch_text.stroke-32"),sQuery(id+"F1.wireOp",EDGE,"E2.sketch_text.stroke-33"),sQuery(id+"F1.wireOp",EDGE,"E2.sketch_text.stroke-34"),sQuery(id+"F1.wireOp",EDGE,"E2.sketch_text.stroke-35"),sQuery(id+"F1.wireOp",EDGE,"E2.sketch_text.stroke-36"),sQuery(id+"F1.wireOp",EDGE,"E2.sketch_text.stroke-37"),sQuery(id+"F1.wireOp",EDGE,"E2.sketch_text.stroke-38"),sQuery(id+"F1.wireOp",EDGE,"E2.sketch_text.stroke-39"),sQuery(id+"F1.wireOp",EDGE,"E2.sketch_text.stroke-40"),sQuery(id+"F1.wireOp",EDGE,"E2.sketch_text.stroke-41"),sQuery(id+"F1.wireOp",EDGE,"E2.sketch_text.stroke-42"),sQuery(id+"F1.wireOp",EDGE,"E2.sketch_text.stroke-43")])],"isStart":false}),makeQuery(id+"F2.opExtrude","CAP_FACE",FACE,{"disambiguationData":[OSD([sQuery(id+"F1.wireOp",EDGE,"E2.sketch_text.stroke-44"),sQuery(id+"F1.wireOp",EDGE,"E2.sketch_text.stroke-45"),sQuery(id+"F1.wireOp",EDGE,"E2.sketch_text.stroke-46"),sQuery(id+"F1.wireOp",EDGE,"E2.sketch_text.stroke-47"),sQuery(id+"F1.wireOp",EDGE,"E2.sketch_text.stroke-48"),sQuery(id+"F1.wireOp",EDGE,"E2.sketch_text.stroke-49"),sQuery(id+"F1.wireOp",EDGE,"E2.sketch_text.stroke-50"),sQuery(id+"F1.wireOp",EDGE,"E2.sketch_text.stroke-51"),sQuery(id+"F1.wireOp",EDGE,"E2.sketch_text.stroke-52"),sQuery(id+"F1.wireOp",EDGE,"E2.sketch_text.stroke-53"),sQuery(id+"F1.wireOp",EDGE,"E2.sketch_text.stroke-54"),sQuery(id+"F1.wireOp",EDGE,"E2.sketch_text.stroke-55"),sQuery(id+"F1.wireOp",EDGE,"E2.sketch_text.stroke-56"),sQuery(id+"F1.wireOp",EDGE,"E2.sketch_text.stroke-57"),sQuery(id+"F1.wireOp",EDGE,"E2.sketch_text.stroke-58"),sQuery(id+"F1.wireOp",EDGE,"E2.sketch_text.stroke-59"),sQuery(id+"F1.wireOp",EDGE,"E2.sketch_text.stroke-60")])],"isStart":false}),makeQuery(id+"F2.opExtrude","CAP_FACE",FACE,{"disambiguationData":[OSD([sQuery(id+"F1.wireOp",EDGE,"E2.sketch_text.stroke-61"),sQuery(id+"F1.wireOp",EDGE,"E2.sketch_text.stroke-62"),sQuery(id+"F1.wireOp",EDGE,"E2.sketch_text.stroke-63"),sQuery(id+"F1.wireOp",EDGE,"E2.sketch_text.stroke-64"),sQuery(id+"F1.wireOp",EDGE,"E2.sketch_text.stroke-65"),sQuery(id+"F1.wireOp",EDGE,"E2.sketch_text.stroke-66"),sQuery(id+"F1.wireOp",EDGE,"E2.sketch_text.stroke-67"),sQuery(id+"F1.wireOp",EDGE,"E2.sketch_text.stroke-68"),sQuery(id+"F1.wireOp",EDGE,"E2.sketch_text.stroke-69"),sQuery(id+"F1.wireOp",EDGE,"E2.sketch_text.stroke-70"),sQuery(id+"F1.wireOp",EDGE,"E2.sketch_text.stroke-71"),sQuery(id+"F1.wireOp",EDGE,"E2.sketch_text.stroke-72"),sQuery(id+"F1.wireOp",EDGE,"E2.sketch_text.stroke-73"),sQuery(id+"F1.wireOp",EDGE,"E2.sketch_text.stroke-74"),sQuery(id+"F1.wireOp",EDGE,"E2.sketch_text.stroke-75"),sQuery(id+"F1.wireOp",EDGE,"E2.sketch_text.stroke-76"),sQuery(id+"F1.wireOp",EDGE,"E2.sketch_text.stroke-77")])],"isStart":false}),makeQuery(id+"F2.opExtrude","CAP_FACE",FACE,{"disambiguationData":[OSD([sQuery(id+"F1.wireOp",EDGE,"E2.sketch_text.stroke-78"),sQuery(id+"F1.wireOp",EDGE,"E2.sketch_text.stroke-79"),sQuery(id+"F1.wireOp",EDGE,"E2.sketch_text.stroke-80"),sQuery(id+"F1.wireOp",EDGE,"E2.sketch_text.stroke-81"),sQuery(id+"F1.wireOp",EDGE,"E2.sketch_text.stroke-82"),sQuery(id+"F1.wireOp",EDGE,"E2.sketch_text.stroke-83"),sQuery(id+"F1.wireOp",EDGE,"E2.sketch_text.stroke-84"),sQuery(id+"F1.wireOp",EDGE,"E2.sketch_text.stroke-85"),sQuery(id+"F1.wireOp",EDGE,"E2.sketch_text.stroke-86"),sQuery(id+"F1.wireOp",EDGE,"E2.sketch_text.stroke-87"),sQuery(id+"F1.wireOp",EDGE,"E2.sketch_text.stroke-88"),sQuery(id+"F1.wireOp",EDGE,"E2.sketch_text.stroke-89"),sQuery(id+"F1.wireOp",EDGE,"E2.sketch_text.stroke-90"),sQuery(id+"F1.wireOp",EDGE,"E2.sketch_text.stroke-91"),sQuery(id+"F1.wireOp",EDGE,"E2.sketch_text.stroke-92"),sQuery(id+"F1.wireOp",EDGE,"E2.sketch_text.stroke-93"),sQuery(id+"F1.wireOp",EDGE,"E2.sketch_text.stroke-94"),sQuery(id+"F1.wireOp",EDGE,"E2.sketch_text.stroke-95")])],"isStart":false}),makeQuery(id+"F2.opExtrude","CAP_FACE",FACE,{"disambiguationData":[OSD([sQuery(id+"F1.wireOp",EDGE,"E2.sketch_text.stroke-96"),sQuery(id+"F1.wireOp",EDGE,"E2.sketch_text.stroke-97"),sQuery(id+"F1.wireOp",EDGE,"E2.sketch_text.stroke-98"),sQuery(id+"F1.wireOp",EDGE,"E2.sketch_text.stroke-99"),sQuery(id+"F1.wireOp",EDGE,"E2.sketch_text.stroke-100"),sQuery(id+"F1.wireOp",EDGE,"E2.sketch_text.stroke-101"),sQuery(id+"F1.wireOp",EDGE,"E2.sketch_text.stroke-102"),sQuery(id+"F1.wireOp",EDGE,"E2.sketch_text.stroke-103"),sQuery(id+"F1.wireOp",EDGE,"E2.sketch_text.stroke-104"),sQuery(id+"F1.wireOp",EDGE,"E2.sketch_text.stroke-105"),sQuery(id+"F1.wireOp",EDGE,"E2.sketch_text.stroke-106"),sQuery(id+"F1.wireOp",EDGE,"E2.sketch_text.stroke-107"),sQuery(id+"F1.wireOp",EDGE,"E2.sketch_text.stroke-108"),sQuery(id+"F1.wireOp",EDGE,"E2.sketch_text.stroke-109"),sQuery(id+"F1.wireOp",EDGE,"E2.sketch_text.stroke-110"),sQuery(id+"F1.wireOp",EDGE,"E2.sketch_text.stroke-111"),sQuery(id+"F1.wireOp",EDGE,"E2.sketch_text.stroke-112")])],"isStart":false})]})});
            var Q4;
            Q4=makeQuery(id+"F6.boolean.opBoolean","SPLIT",FACE,{"disambiguationData":[TD([makeQuery(id+"F6.opExtrude","SWEPT_FACE",FACE,{"disambiguationData":[OSD([sQuery(id+"F5.wireOp",EDGE,"E3.sketch_text.stroke-216")])]})])],"derivedFrom":makeQuery(id+"F3.opBoolean","MERGE",FACE,{"derivedFrom":[makeQuery(id+"F2.opExtrude","CAP_FACE",FACE,{"disambiguationData":[OSD([sQuery(id+"F0.wireOp",EDGE,"E0.bottom"),sQuery(id+"F0.wireOp",EDGE,"E0.top"),sQuery(id+"F0.wireOp",EDGE,"E0.left"),sQuery(id+"F0.wireOp",EDGE,"E0.right"),sQuery(id+"F0.wireOp",EDGE,"E1.0"),sQuery(id+"F0.wireOp",EDGE,"E1.1"),sQuery(id+"F0.wireOp",EDGE,"E1.2"),sQuery(id+"F0.wireOp",EDGE,"E1.3")])],"isStart":false}),makeQuery(id+"F2.opExtrude","CAP_FACE",FACE,{"disambiguationData":[OSD([sQuery(id+"F1.wireOp",EDGE,"E2.sketch_text.stroke-0"),sQuery(id+"F1.wireOp",EDGE,"E2.sketch_text.stroke-1"),sQuery(id+"F1.wireOp",EDGE,"E2.sketch_text.stroke-2"),sQuery(id+"F1.wireOp",EDGE,"E2.sketch_text.stroke-3"),sQuery(id+"F1.wireOp",EDGE,"E2.sketch_text.stroke-4"),sQuery(id+"F1.wireOp",EDGE,"E2.sketch_text.stroke-5"),sQuery(id+"F1.wireOp",EDGE,"E2.sketch_text.stroke-6"),sQuery(id+"F1.wireOp",EDGE,"E2.sketch_text.stroke-7"),sQuery(id+"F1.wireOp",EDGE,"E2.sketch_text.stroke-8"),sQuery(id+"F1.wireOp",EDGE,"E2.sketch_text.stroke-9"),sQuery(id+"F1.wireOp",EDGE,"E2.sketch_text.stroke-10"),sQuery(id+"F1.wireOp",EDGE,"E2.sketch_text.stroke-11"),sQuery(id+"F1.wireOp",EDGE,"E2.sketch_text.stroke-12"),sQuery(id+"F1.wireOp",EDGE,"E2.sketch_text.stroke-13"),sQuery(id+"F1.wireOp",EDGE,"E2.sketch_text.stroke-14"),sQuery(id+"F1.wireOp",EDGE,"E2.sketch_text.stroke-15"),sQuery(id+"F1.wireOp",EDGE,"E2.sketch_text.stroke-16"),sQuery(id+"F1.wireOp",EDGE,"E2.sketch_text.stroke-17"),sQuery(id+"F1.wireOp",EDGE,"E2.sketch_text.stroke-18")])],"isStart":false}),makeQuery(id+"F2.opExtrude","CAP_FACE",FACE,{"disambiguationData":[OSD([sQuery(id+"F1.wireOp",EDGE,"E2.sketch_text.stroke-19"),sQuery(id+"F1.wireOp",EDGE,"E2.sketch_text.stroke-20"),sQuery(id+"F1.wireOp",EDGE,"E2.sketch_text.stroke-21"),sQuery(id+"F1.wireOp",EDGE,"E2.sketch_text.stroke-22"),sQuery(id+"F1.wireOp",EDGE,"E2.sketch_text.stroke-23"),sQuery(id+"F1.wireOp",EDGE,"E2.sketch_text.stroke-24"),sQuery(id+"F1.wireOp",EDGE,"E2.sketch_text.stroke-25"),sQuery(id+"F1.wireOp",EDGE,"E2.sketch_text.stroke-26"),sQuery(id+"F1.wireOp",EDGE,"E2.sketch_text.stroke-27"),sQuery(id+"F1.wireOp",EDGE,"E2.sketch_text.stroke-28"),sQuery(id+"F1.wireOp",EDGE,"E2.sketch_text.stroke-29"),sQuery(id+"F1.wireOp",EDGE,"E2.sketch_text.stroke-30"),sQuery(id+"F1.wireOp",EDGE,"E2.sketch_text.stroke-31"),sQuery(id+"F1.wireOp",EDGE,"E2.sketch_text.stroke-32"),sQuery(id+"F1.wireOp",EDGE,"E2.sketch_text.stroke-33"),sQuery(id+"F1.wireOp",EDGE,"E2.sketch_text.stroke-34"),sQuery(id+"F1.wireOp",EDGE,"E2.sketch_text.stroke-35"),sQuery(id+"F1.wireOp",EDGE,"E2.sketch_text.stroke-36"),sQuery(id+"F1.wireOp",EDGE,"E2.sketch_text.stroke-37"),sQuery(id+"F1.wireOp",EDGE,"E2.sketch_text.stroke-38"),sQuery(id+"F1.wireOp",EDGE,"E2.sketch_text.stroke-39"),sQuery(id+"F1.wireOp",EDGE,"E2.sketch_text.stroke-40"),sQuery(id+"F1.wireOp",EDGE,"E2.sketch_text.stroke-41"),sQuery(id+"F1.wireOp",EDGE,"E2.sketch_text.stroke-42"),sQuery(id+"F1.wireOp",EDGE,"E2.sketch_text.stroke-43")])],"isStart":false}),makeQuery(id+"F2.opExtrude","CAP_FACE",FACE,{"disambiguationData":[OSD([sQuery(id+"F1.wireOp",EDGE,"E2.sketch_text.stroke-44"),sQuery(id+"F1.wireOp",EDGE,"E2.sketch_text.stroke-45"),sQuery(id+"F1.wireOp",EDGE,"E2.sketch_text.stroke-46"),sQuery(id+"F1.wireOp",EDGE,"E2.sketch_text.stroke-47"),sQuery(id+"F1.wireOp",EDGE,"E2.sketch_text.stroke-48"),sQuery(id+"F1.wireOp",EDGE,"E2.sketch_text.stroke-49"),sQuery(id+"F1.wireOp",EDGE,"E2.sketch_text.stroke-50"),sQuery(id+"F1.wireOp",EDGE,"E2.sketch_text.stroke-51"),sQuery(id+"F1.wireOp",EDGE,"E2.sketch_text.stroke-52"),sQuery(id+"F1.wireOp",EDGE,"E2.sketch_text.stroke-53"),sQuery(id+"F1.wireOp",EDGE,"E2.sketch_text.stroke-54"),sQuery(id+"F1.wireOp",EDGE,"E2.sketch_text.stroke-55"),sQuery(id+"F1.wireOp",EDGE,"E2.sketch_text.stroke-56"),sQuery(id+"F1.wireOp",EDGE,"E2.sketch_text.stroke-57"),sQuery(id+"F1.wireOp",EDGE,"E2.sketch_text.stroke-58"),sQuery(id+"F1.wireOp",EDGE,"E2.sketch_text.stroke-59"),sQuery(id+"F1.wireOp",EDGE,"E2.sketch_text.stroke-60")])],"isStart":false}),makeQuery(id+"F2.opExtrude","CAP_FACE",FACE,{"disambiguationData":[OSD([sQuery(id+"F1.wireOp",EDGE,"E2.sketch_text.stroke-61"),sQuery(id+"F1.wireOp",EDGE,"E2.sketch_text.stroke-62"),sQuery(id+"F1.wireOp",EDGE,"E2.sketch_text.stroke-63"),sQuery(id+"F1.wireOp",EDGE,"E2.sketch_text.stroke-64"),sQuery(id+"F1.wireOp",EDGE,"E2.sketch_text.stroke-65"),sQuery(id+"F1.wireOp",EDGE,"E2.sketch_text.stroke-66"),sQuery(id+"F1.wireOp",EDGE,"E2.sketch_text.stroke-67"),sQuery(id+"F1.wireOp",EDGE,"E2.sketch_text.stroke-68"),sQuery(id+"F1.wireOp",EDGE,"E2.sketch_text.stroke-69"),sQuery(id+"F1.wireOp",EDGE,"E2.sketch_text.stroke-70"),sQuery(id+"F1.wireOp",EDGE,"E2.sketch_text.stroke-71"),sQuery(id+"F1.wireOp",EDGE,"E2.sketch_text.stroke-72"),sQuery(id+"F1.wireOp",EDGE,"E2.sketch_text.stroke-73"),sQuery(id+"F1.wireOp",EDGE,"E2.sketch_text.stroke-74"),sQuery(id+"F1.wireOp",EDGE,"E2.sketch_text.stroke-75"),sQuery(id+"F1.wireOp",EDGE,"E2.sketch_text.stroke-76"),sQuery(id+"F1.wireOp",EDGE,"E2.sketch_text.stroke-77")])],"isStart":false}),makeQuery(id+"F2.opExtrude","CAP_FACE",FACE,{"disambiguationData":[OSD([sQuery(id+"F1.wireOp",EDGE,"E2.sketch_text.stroke-78"),sQuery(id+"F1.wireOp",EDGE,"E2.sketch_text.stroke-79"),sQuery(id+"F1.wireOp",EDGE,"E2.sketch_text.stroke-80"),sQuery(id+"F1.wireOp",EDGE,"E2.sketch_text.stroke-81"),sQuery(id+"F1.wireOp",EDGE,"E2.sketch_text.stroke-82"),sQuery(id+"F1.wireOp",EDGE,"E2.sketch_text.stroke-83"),sQuery(id+"F1.wireOp",EDGE,"E2.sketch_text.stroke-84"),sQuery(id+"F1.wireOp",EDGE,"E2.sketch_text.stroke-85"),sQuery(id+"F1.wireOp",EDGE,"E2.sketch_text.stroke-86"),sQuery(id+"F1.wireOp",EDGE,"E2.sketch_text.stroke-87"),sQuery(id+"F1.wireOp",EDGE,"E2.sketch_text.stroke-88"),sQuery(id+"F1.wireOp",EDGE,"E2.sketch_text.stroke-89"),sQuery(id+"F1.wireOp",EDGE,"E2.sketch_text.stroke-90"),sQuery(id+"F1.wireOp",EDGE,"E2.sketch_text.stroke-91"),sQuery(id+"F1.wireOp",EDGE,"E2.sketch_text.stroke-92"),sQuery(id+"F1.wireOp",EDGE,"E2.sketch_text.stroke-93"),sQuery(id+"F1.wireOp",EDGE,"E2.sketch_text.stroke-94"),sQuery(id+"F1.wireOp",EDGE,"E2.sketch_text.stroke-95")])],"isStart":false}),makeQuery(id+"F2.opExtrude","CAP_FACE",FACE,{"disambiguationData":[OSD([sQuery(id+"F1.wireOp",EDGE,"E2.sketch_text.stroke-96"),sQuery(id+"F1.wireOp",EDGE,"E2.sketch_text.stroke-97"),sQuery(id+"F1.wireOp",EDGE,"E2.sketch_text.stroke-98"),sQuery(id+"F1.wireOp",EDGE,"E2.sketch_text.stroke-99"),sQuery(id+"F1.wireOp",EDGE,"E2.sketch_text.stroke-100"),sQuery(id+"F1.wireOp",EDGE,"E2.sketch_text.stroke-101"),sQuery(id+"F1.wireOp",EDGE,"E2.sketch_text.stroke-102"),sQuery(id+"F1.wireOp",EDGE,"E2.sketch_text.stroke-103"),sQuery(id+"F1.wireOp",EDGE,"E2.sketch_text.stroke-104"),sQuery(id+"F1.wireOp",EDGE,"E2.sketch_text.stroke-105"),sQuery(id+"F1.wireOp",EDGE,"E2.sketch_text.stroke-106"),sQuery(id+"F1.wireOp",EDGE,"E2.sketch_text.stroke-107"),sQuery(id+"F1.wireOp",EDGE,"E2.sketch_text.stroke-108"),sQuery(id+"F1.wireOp",EDGE,"E2.sketch_text.stroke-109"),sQuery(id+"F1.wireOp",EDGE,"E2.sketch_text.stroke-110"),sQuery(id+"F1.wireOp",EDGE,"E2.sketch_text.stroke-111"),sQuery(id+"F1.wireOp",EDGE,"E2.sketch_text.stroke-112")])],"isStart":false})]})});
            var Q5;
            Q5=makeQuery(id+"F6.boolean.opBoolean","SPLIT",FACE,{"disambiguationData":[TD([makeQuery(id+"F6.opExtrude","SWEPT_FACE",FACE,{"disambiguationData":[OSD([sQuery(id+"F5.wireOp",EDGE,"E3.sketch_text.stroke-310")])]})])],"derivedFrom":makeQuery(id+"F3.opBoolean","MERGE",FACE,{"derivedFrom":[makeQuery(id+"F2.opExtrude","CAP_FACE",FACE,{"disambiguationData":[OSD([sQuery(id+"F0.wireOp",EDGE,"E0.bottom"),sQuery(id+"F0.wireOp",EDGE,"E0.top"),sQuery(id+"F0.wireOp",EDGE,"E0.left"),sQuery(id+"F0.wireOp",EDGE,"E0.right"),sQuery(id+"F0.wireOp",EDGE,"E1.0"),sQuery(id+"F0.wireOp",EDGE,"E1.1"),sQuery(id+"F0.wireOp",EDGE,"E1.2"),sQuery(id+"F0.wireOp",EDGE,"E1.3")])],"isStart":false}),makeQuery(id+"F2.opExtrude","CAP_FACE",FACE,{"disambiguationData":[OSD([sQuery(id+"F1.wireOp",EDGE,"E2.sketch_text.stroke-0"),sQuery(id+"F1.wireOp",EDGE,"E2.sketch_text.stroke-1"),sQuery(id+"F1.wireOp",EDGE,"E2.sketch_text.stroke-2"),sQuery(id+"F1.wireOp",EDGE,"E2.sketch_text.stroke-3"),sQuery(id+"F1.wireOp",EDGE,"E2.sketch_text.stroke-4"),sQuery(id+"F1.wireOp",EDGE,"E2.sketch_text.stroke-5"),sQuery(id+"F1.wireOp",EDGE,"E2.sketch_text.stroke-6"),sQuery(id+"F1.wireOp",EDGE,"E2.sketch_text.stroke-7"),sQuery(id+"F1.wireOp",EDGE,"E2.sketch_text.stroke-8"),sQuery(id+"F1.wireOp",EDGE,"E2.sketch_text.stroke-9"),sQuery(id+"F1.wireOp",EDGE,"E2.sketch_text.stroke-10"),sQuery(id+"F1.wireOp",EDGE,"E2.sketch_text.stroke-11"),sQuery(id+"F1.wireOp",EDGE,"E2.sketch_text.stroke-12"),sQuery(id+"F1.wireOp",EDGE,"E2.sketch_text.stroke-13"),sQuery(id+"F1.wireOp",EDGE,"E2.sketch_text.stroke-14"),sQuery(id+"F1.wireOp",EDGE,"E2.sketch_text.stroke-15"),sQuery(id+"F1.wireOp",EDGE,"E2.sketch_text.stroke-16"),sQuery(id+"F1.wireOp",EDGE,"E2.sketch_text.stroke-17"),sQuery(id+"F1.wireOp",EDGE,"E2.sketch_text.stroke-18")])],"isStart":false}),makeQuery(id+"F2.opExtrude","CAP_FACE",FACE,{"disambiguationData":[OSD([sQuery(id+"F1.wireOp",EDGE,"E2.sketch_text.stroke-19"),sQuery(id+"F1.wireOp",EDGE,"E2.sketch_text.stroke-20"),sQuery(id+"F1.wireOp",EDGE,"E2.sketch_text.stroke-21"),sQuery(id+"F1.wireOp",EDGE,"E2.sketch_text.stroke-22"),sQuery(id+"F1.wireOp",EDGE,"E2.sketch_text.stroke-23"),sQuery(id+"F1.wireOp",EDGE,"E2.sketch_text.stroke-24"),sQuery(id+"F1.wireOp",EDGE,"E2.sketch_text.stroke-25"),sQuery(id+"F1.wireOp",EDGE,"E2.sketch_text.stroke-26"),sQuery(id+"F1.wireOp",EDGE,"E2.sketch_text.stroke-27"),sQuery(id+"F1.wireOp",EDGE,"E2.sketch_text.stroke-28"),sQuery(id+"F1.wireOp",EDGE,"E2.sketch_text.stroke-29"),sQuery(id+"F1.wireOp",EDGE,"E2.sketch_text.stroke-30"),sQuery(id+"F1.wireOp",EDGE,"E2.sketch_text.stroke-31"),sQuery(id+"F1.wireOp",EDGE,"E2.sketch_text.stroke-32"),sQuery(id+"F1.wireOp",EDGE,"E2.sketch_text.stroke-33"),sQuery(id+"F1.wireOp",EDGE,"E2.sketch_text.stroke-34"),sQuery(id+"F1.wireOp",EDGE,"E2.sketch_text.stroke-35"),sQuery(id+"F1.wireOp",EDGE,"E2.sketch_text.stroke-36"),sQuery(id+"F1.wireOp",EDGE,"E2.sketch_text.stroke-37"),sQuery(id+"F1.wireOp",EDGE,"E2.sketch_text.stroke-38"),sQuery(id+"F1.wireOp",EDGE,"E2.sketch_text.stroke-39"),sQuery(id+"F1.wireOp",EDGE,"E2.sketch_text.stroke-40"),sQuery(id+"F1.wireOp",EDGE,"E2.sketch_text.stroke-41"),sQuery(id+"F1.wireOp",EDGE,"E2.sketch_text.stroke-42"),sQuery(id+"F1.wireOp",EDGE,"E2.sketch_text.stroke-43")])],"isStart":false}),makeQuery(id+"F2.opExtrude","CAP_FACE",FACE,{"disambiguationData":[OSD([sQuery(id+"F1.wireOp",EDGE,"E2.sketch_text.stroke-44"),sQuery(id+"F1.wireOp",EDGE,"E2.sketch_text.stroke-45"),sQuery(id+"F1.wireOp",EDGE,"E2.sketch_text.stroke-46"),sQuery(id+"F1.wireOp",EDGE,"E2.sketch_text.stroke-47"),sQuery(id+"F1.wireOp",EDGE,"E2.sketch_text.stroke-48"),sQuery(id+"F1.wireOp",EDGE,"E2.sketch_text.stroke-49"),sQuery(id+"F1.wireOp",EDGE,"E2.sketch_text.stroke-50"),sQuery(id+"F1.wireOp",EDGE,"E2.sketch_text.stroke-51"),sQuery(id+"F1.wireOp",EDGE,"E2.sketch_text.stroke-52"),sQuery(id+"F1.wireOp",EDGE,"E2.sketch_text.stroke-53"),sQuery(id+"F1.wireOp",EDGE,"E2.sketch_text.stroke-54"),sQuery(id+"F1.wireOp",EDGE,"E2.sketch_text.stroke-55"),sQuery(id+"F1.wireOp",EDGE,"E2.sketch_text.stroke-56"),sQuery(id+"F1.wireOp",EDGE,"E2.sketch_text.stroke-57"),sQuery(id+"F1.wireOp",EDGE,"E2.sketch_text.stroke-58"),sQuery(id+"F1.wireOp",EDGE,"E2.sketch_text.stroke-59"),sQuery(id+"F1.wireOp",EDGE,"E2.sketch_text.stroke-60")])],"isStart":false}),makeQuery(id+"F2.opExtrude","CAP_FACE",FACE,{"disambiguationData":[OSD([sQuery(id+"F1.wireOp",EDGE,"E2.sketch_text.stroke-61"),sQuery(id+"F1.wireOp",EDGE,"E2.sketch_text.stroke-62"),sQuery(id+"F1.wireOp",EDGE,"E2.sketch_text.stroke-63"),sQuery(id+"F1.wireOp",EDGE,"E2.sketch_text.stroke-64"),sQuery(id+"F1.wireOp",EDGE,"E2.sketch_text.stroke-65"),sQuery(id+"F1.wireOp",EDGE,"E2.sketch_text.stroke-66"),sQuery(id+"F1.wireOp",EDGE,"E2.sketch_text.stroke-67"),sQuery(id+"F1.wireOp",EDGE,"E2.sketch_text.stroke-68"),sQuery(id+"F1.wireOp",EDGE,"E2.sketch_text.stroke-69"),sQuery(id+"F1.wireOp",EDGE,"E2.sketch_text.stroke-70"),sQuery(id+"F1.wireOp",EDGE,"E2.sketch_text.stroke-71"),sQuery(id+"F1.wireOp",EDGE,"E2.sketch_text.stroke-72"),sQuery(id+"F1.wireOp",EDGE,"E2.sketch_text.stroke-73"),sQuery(id+"F1.wireOp",EDGE,"E2.sketch_text.stroke-74"),sQuery(id+"F1.wireOp",EDGE,"E2.sketch_text.stroke-75"),sQuery(id+"F1.wireOp",EDGE,"E2.sketch_text.stroke-76"),sQuery(id+"F1.wireOp",EDGE,"E2.sketch_text.stroke-77")])],"isStart":false}),makeQuery(id+"F2.opExtrude","CAP_FACE",FACE,{"disambiguationData":[OSD([sQuery(id+"F1.wireOp",EDGE,"E2.sketch_text.stroke-78"),sQuery(id+"F1.wireOp",EDGE,"E2.sketch_text.stroke-79"),sQuery(id+"F1.wireOp",EDGE,"E2.sketch_text.stroke-80"),sQuery(id+"F1.wireOp",EDGE,"E2.sketch_text.stroke-81"),sQuery(id+"F1.wireOp",EDGE,"E2.sketch_text.stroke-82"),sQuery(id+"F1.wireOp",EDGE,"E2.sketch_text.stroke-83"),sQuery(id+"F1.wireOp",EDGE,"E2.sketch_text.stroke-84"),sQuery(id+"F1.wireOp",EDGE,"E2.sketch_text.stroke-85"),sQuery(id+"F1.wireOp",EDGE,"E2.sketch_text.stroke-86"),sQuery(id+"F1.wireOp",EDGE,"E2.sketch_text.stroke-87"),sQuery(id+"F1.wireOp",EDGE,"E2.sketch_text.stroke-88"),sQuery(id+"F1.wireOp",EDGE,"E2.sketch_text.stroke-89"),sQuery(id+"F1.wireOp",EDGE,"E2.sketch_text.stroke-90"),sQuery(id+"F1.wireOp",EDGE,"E2.sketch_text.stroke-91"),sQuery(id+"F1.wireOp",EDGE,"E2.sketch_text.stroke-92"),sQuery(id+"F1.wireOp",EDGE,"E2.sketch_text.stroke-93"),sQuery(id+"F1.wireOp",EDGE,"E2.sketch_text.stroke-94"),sQuery(id+"F1.wireOp",EDGE,"E2.sketch_text.stroke-95")])],"isStart":false}),makeQuery(id+"F2.opExtrude","CAP_FACE",FACE,{"disambiguationData":[OSD([sQuery(id+"F1.wireOp",EDGE,"E2.sketch_text.stroke-96"),sQuery(id+"F1.wireOp",EDGE,"E2.sketch_text.stroke-97"),sQuery(id+"F1.wireOp",EDGE,"E2.sketch_text.stroke-98"),sQuery(id+"F1.wireOp",EDGE,"E2.sketch_text.stroke-99"),sQuery(id+"F1.wireOp",EDGE,"E2.sketch_text.stroke-100"),sQuery(id+"F1.wireOp",EDGE,"E2.sketch_text.stroke-101"),sQuery(id+"F1.wireOp",EDGE,"E2.sketch_text.stroke-102"),sQuery(id+"F1.wireOp",EDGE,"E2.sketch_text.stroke-103"),sQuery(id+"F1.wireOp",EDGE,"E2.sketch_text.stroke-104"),sQuery(id+"F1.wireOp",EDGE,"E2.sketch_text.stroke-105"),sQuery(id+"F1.wireOp",EDGE,"E2.sketch_text.stroke-106"),sQuery(id+"F1.wireOp",EDGE,"E2.sketch_text.stroke-107"),sQuery(id+"F1.wireOp",EDGE,"E2.sketch_text.stroke-108"),sQuery(id+"F1.wireOp",EDGE,"E2.sketch_text.stroke-109"),sQuery(id+"F1.wireOp",EDGE,"E2.sketch_text.stroke-110"),sQuery(id+"F1.wireOp",EDGE,"E2.sketch_text.stroke-111"),sQuery(id+"F1.wireOp",EDGE,"E2.sketch_text.stroke-112")])],"isStart":false})]})});
            var Q6;
            Q6=makeQuery(id+"F6.boolean.opBoolean","SPLIT",FACE,{"disambiguationData":[TD([makeQuery(id+"F6.opExtrude","SWEPT_FACE",FACE,{"disambiguationData":[OSD([sQuery(id+"F5.wireOp",EDGE,"E3.sketch_text.stroke-346")])]})])],"derivedFrom":makeQuery(id+"F3.opBoolean","MERGE",FACE,{"derivedFrom":[makeQuery(id+"F2.opExtrude","CAP_FACE",FACE,{"disambiguationData":[OSD([sQuery(id+"F0.wireOp",EDGE,"E0.bottom"),sQuery(id+"F0.wireOp",EDGE,"E0.top"),sQuery(id+"F0.wireOp",EDGE,"E0.left"),sQuery(id+"F0.wireOp",EDGE,"E0.right"),sQuery(id+"F0.wireOp",EDGE,"E1.0"),sQuery(id+"F0.wireOp",EDGE,"E1.1"),sQuery(id+"F0.wireOp",EDGE,"E1.2"),sQuery(id+"F0.wireOp",EDGE,"E1.3")])],"isStart":false}),makeQuery(id+"F2.opExtrude","CAP_FACE",FACE,{"disambiguationData":[OSD([sQuery(id+"F1.wireOp",EDGE,"E2.sketch_text.stroke-0"),sQuery(id+"F1.wireOp",EDGE,"E2.sketch_text.stroke-1"),sQuery(id+"F1.wireOp",EDGE,"E2.sketch_text.stroke-2"),sQuery(id+"F1.wireOp",EDGE,"E2.sketch_text.stroke-3"),sQuery(id+"F1.wireOp",EDGE,"E2.sketch_text.stroke-4"),sQuery(id+"F1.wireOp",EDGE,"E2.sketch_text.stroke-5"),sQuery(id+"F1.wireOp",EDGE,"E2.sketch_text.stroke-6"),sQuery(id+"F1.wireOp",EDGE,"E2.sketch_text.stroke-7"),sQuery(id+"F1.wireOp",EDGE,"E2.sketch_text.stroke-8"),sQuery(id+"F1.wireOp",EDGE,"E2.sketch_text.stroke-9"),sQuery(id+"F1.wireOp",EDGE,"E2.sketch_text.stroke-10"),sQuery(id+"F1.wireOp",EDGE,"E2.sketch_text.stroke-11"),sQuery(id+"F1.wireOp",EDGE,"E2.sketch_text.stroke-12"),sQuery(id+"F1.wireOp",EDGE,"E2.sketch_text.stroke-13"),sQuery(id+"F1.wireOp",EDGE,"E2.sketch_text.stroke-14"),sQuery(id+"F1.wireOp",EDGE,"E2.sketch_text.stroke-15"),sQuery(id+"F1.wireOp",EDGE,"E2.sketch_text.stroke-16"),sQuery(id+"F1.wireOp",EDGE,"E2.sketch_text.stroke-17"),sQuery(id+"F1.wireOp",EDGE,"E2.sketch_text.stroke-18")])],"isStart":false}),makeQuery(id+"F2.opExtrude","CAP_FACE",FACE,{"disambiguationData":[OSD([sQuery(id+"F1.wireOp",EDGE,"E2.sketch_text.stroke-19"),sQuery(id+"F1.wireOp",EDGE,"E2.sketch_text.stroke-20"),sQuery(id+"F1.wireOp",EDGE,"E2.sketch_text.stroke-21"),sQuery(id+"F1.wireOp",EDGE,"E2.sketch_text.stroke-22"),sQuery(id+"F1.wireOp",EDGE,"E2.sketch_text.stroke-23"),sQuery(id+"F1.wireOp",EDGE,"E2.sketch_text.stroke-24"),sQuery(id+"F1.wireOp",EDGE,"E2.sketch_text.stroke-25"),sQuery(id+"F1.wireOp",EDGE,"E2.sketch_text.stroke-26"),sQuery(id+"F1.wireOp",EDGE,"E2.sketch_text.stroke-27"),sQuery(id+"F1.wireOp",EDGE,"E2.sketch_text.stroke-28"),sQuery(id+"F1.wireOp",EDGE,"E2.sketch_text.stroke-29"),sQuery(id+"F1.wireOp",EDGE,"E2.sketch_text.stroke-30"),sQuery(id+"F1.wireOp",EDGE,"E2.sketch_text.stroke-31"),sQuery(id+"F1.wireOp",EDGE,"E2.sketch_text.stroke-32"),sQuery(id+"F1.wireOp",EDGE,"E2.sketch_text.stroke-33"),sQuery(id+"F1.wireOp",EDGE,"E2.sketch_text.stroke-34"),sQuery(id+"F1.wireOp",EDGE,"E2.sketch_text.stroke-35"),sQuery(id+"F1.wireOp",EDGE,"E2.sketch_text.stroke-36"),sQuery(id+"F1.wireOp",EDGE,"E2.sketch_text.stroke-37"),sQuery(id+"F1.wireOp",EDGE,"E2.sketch_text.stroke-38"),sQuery(id+"F1.wireOp",EDGE,"E2.sketch_text.stroke-39"),sQuery(id+"F1.wireOp",EDGE,"E2.sketch_text.stroke-40"),sQuery(id+"F1.wireOp",EDGE,"E2.sketch_text.stroke-41"),sQuery(id+"F1.wireOp",EDGE,"E2.sketch_text.stroke-42"),sQuery(id+"F1.wireOp",EDGE,"E2.sketch_text.stroke-43")])],"isStart":false}),makeQuery(id+"F2.opExtrude","CAP_FACE",FACE,{"disambiguationData":[OSD([sQuery(id+"F1.wireOp",EDGE,"E2.sketch_text.stroke-44"),sQuery(id+"F1.wireOp",EDGE,"E2.sketch_text.stroke-45"),sQuery(id+"F1.wireOp",EDGE,"E2.sketch_text.stroke-46"),sQuery(id+"F1.wireOp",EDGE,"E2.sketch_text.stroke-47"),sQuery(id+"F1.wireOp",EDGE,"E2.sketch_text.stroke-48"),sQuery(id+"F1.wireOp",EDGE,"E2.sketch_text.stroke-49"),sQuery(id+"F1.wireOp",EDGE,"E2.sketch_text.stroke-50"),sQuery(id+"F1.wireOp",EDGE,"E2.sketch_text.stroke-51"),sQuery(id+"F1.wireOp",EDGE,"E2.sketch_text.stroke-52"),sQuery(id+"F1.wireOp",EDGE,"E2.sketch_text.stroke-53"),sQuery(id+"F1.wireOp",EDGE,"E2.sketch_text.stroke-54"),sQuery(id+"F1.wireOp",EDGE,"E2.sketch_text.stroke-55"),sQuery(id+"F1.wireOp",EDGE,"E2.sketch_text.stroke-56"),sQuery(id+"F1.wireOp",EDGE,"E2.sketch_text.stroke-57"),sQuery(id+"F1.wireOp",EDGE,"E2.sketch_text.stroke-58"),sQuery(id+"F1.wireOp",EDGE,"E2.sketch_text.stroke-59"),sQuery(id+"F1.wireOp",EDGE,"E2.sketch_text.stroke-60")])],"isStart":false}),makeQuery(id+"F2.opExtrude","CAP_FACE",FACE,{"disambiguationData":[OSD([sQuery(id+"F1.wireOp",EDGE,"E2.sketch_text.stroke-61"),sQuery(id+"F1.wireOp",EDGE,"E2.sketch_text.stroke-62"),sQuery(id+"F1.wireOp",EDGE,"E2.sketch_text.stroke-63"),sQuery(id+"F1.wireOp",EDGE,"E2.sketch_text.stroke-64"),sQuery(id+"F1.wireOp",EDGE,"E2.sketch_text.stroke-65"),sQuery(id+"F1.wireOp",EDGE,"E2.sketch_text.stroke-66"),sQuery(id+"F1.wireOp",EDGE,"E2.sketch_text.stroke-67"),sQuery(id+"F1.wireOp",EDGE,"E2.sketch_text.stroke-68"),sQuery(id+"F1.wireOp",EDGE,"E2.sketch_text.stroke-69"),sQuery(id+"F1.wireOp",EDGE,"E2.sketch_text.stroke-70"),sQuery(id+"F1.wireOp",EDGE,"E2.sketch_text.stroke-71"),sQuery(id+"F1.wireOp",EDGE,"E2.sketch_text.stroke-72"),sQuery(id+"F1.wireOp",EDGE,"E2.sketch_text.stroke-73"),sQuery(id+"F1.wireOp",EDGE,"E2.sketch_text.stroke-74"),sQuery(id+"F1.wireOp",EDGE,"E2.sketch_text.stroke-75"),sQuery(id+"F1.wireOp",EDGE,"E2.sketch_text.stroke-76"),sQuery(id+"F1.wireOp",EDGE,"E2.sketch_text.stroke-77")])],"isStart":false}),makeQuery(id+"F2.opExtrude","CAP_FACE",FACE,{"disambiguationData":[OSD([sQuery(id+"F1.wireOp",EDGE,"E2.sketch_text.stroke-78"),sQuery(id+"F1.wireOp",EDGE,"E2.sketch_text.stroke-79"),sQuery(id+"F1.wireOp",EDGE,"E2.sketch_text.stroke-80"),sQuery(id+"F1.wireOp",EDGE,"E2.sketch_text.stroke-81"),sQuery(id+"F1.wireOp",EDGE,"E2.sketch_text.stroke-82"),sQuery(id+"F1.wireOp",EDGE,"E2.sketch_text.stroke-83"),sQuery(id+"F1.wireOp",EDGE,"E2.sketch_text.stroke-84"),sQuery(id+"F1.wireOp",EDGE,"E2.sketch_text.stroke-85"),sQuery(id+"F1.wireOp",EDGE,"E2.sketch_text.stroke-86"),sQuery(id+"F1.wireOp",EDGE,"E2.sketch_text.stroke-87"),sQuery(id+"F1.wireOp",EDGE,"E2.sketch_text.stroke-88"),sQuery(id+"F1.wireOp",EDGE,"E2.sketch_text.stroke-89"),sQuery(id+"F1.wireOp",EDGE,"E2.sketch_text.stroke-90"),sQuery(id+"F1.wireOp",EDGE,"E2.sketch_text.stroke-91"),sQuery(id+"F1.wireOp",EDGE,"E2.sketch_text.stroke-92"),sQuery(id+"F1.wireOp",EDGE,"E2.sketch_text.stroke-93"),sQuery(id+"F1.wireOp",EDGE,"E2.sketch_text.stroke-94"),sQuery(id+"F1.wireOp",EDGE,"E2.sketch_text.stroke-95")])],"isStart":false}),makeQuery(id+"F2.opExtrude","CAP_FACE",FACE,{"disambiguationData":[OSD([sQuery(id+"F1.wireOp",EDGE,"E2.sketch_text.stroke-96"),sQuery(id+"F1.wireOp",EDGE,"E2.sketch_text.stroke-97"),sQuery(id+"F1.wireOp",EDGE,"E2.sketch_text.stroke-98"),sQuery(id+"F1.wireOp",EDGE,"E2.sketch_text.stroke-99"),sQuery(id+"F1.wireOp",EDGE,"E2.sketch_text.stroke-100"),sQuery(id+"F1.wireOp",EDGE,"E2.sketch_text.stroke-101"),sQuery(id+"F1.wireOp",EDGE,"E2.sketch_text.stroke-102"),sQuery(id+"F1.wireOp",EDGE,"E2.sketch_text.stroke-103"),sQuery(id+"F1.wireOp",EDGE,"E2.sketch_text.stroke-104"),sQuery(id+"F1.wireOp",EDGE,"E2.sketch_text.stroke-105"),sQuery(id+"F1.wireOp",EDGE,"E2.sketch_text.stroke-106"),sQuery(id+"F1.wireOp",EDGE,"E2.sketch_text.stroke-107"),sQuery(id+"F1.wireOp",EDGE,"E2.sketch_text.stroke-108"),sQuery(id+"F1.wireOp",EDGE,"E2.sketch_text.stroke-109"),sQuery(id+"F1.wireOp",EDGE,"E2.sketch_text.stroke-110"),sQuery(id+"F1.wireOp",EDGE,"E2.sketch_text.stroke-111"),sQuery(id+"F1.wireOp",EDGE,"E2.sketch_text.stroke-112")])],"isStart":false})]})});
            var Q7;
            Q7=makeQuery(id+"F6.boolean.opBoolean","SPLIT",FACE,{"disambiguationData":[TD([makeQuery(id+"F6.opExtrude","SWEPT_FACE",FACE,{"disambiguationData":[OSD([sQuery(id+"F5.wireOp",EDGE,"E3.sketch_text.stroke-17")])]})])],"derivedFrom":makeQuery(id+"F3.opBoolean","MERGE",FACE,{"derivedFrom":[makeQuery(id+"F2.opExtrude","CAP_FACE",FACE,{"disambiguationData":[OSD([sQuery(id+"F0.wireOp",EDGE,"E0.bottom"),sQuery(id+"F0.wireOp",EDGE,"E0.top"),sQuery(id+"F0.wireOp",EDGE,"E0.left"),sQuery(id+"F0.wireOp",EDGE,"E0.right"),sQuery(id+"F0.wireOp",EDGE,"E1.0"),sQuery(id+"F0.wireOp",EDGE,"E1.1"),sQuery(id+"F0.wireOp",EDGE,"E1.2"),sQuery(id+"F0.wireOp",EDGE,"E1.3")])],"isStart":false}),makeQuery(id+"F2.opExtrude","CAP_FACE",FACE,{"disambiguationData":[OSD([sQuery(id+"F1.wireOp",EDGE,"E2.sketch_text.stroke-0"),sQuery(id+"F1.wireOp",EDGE,"E2.sketch_text.stroke-1"),sQuery(id+"F1.wireOp",EDGE,"E2.sketch_text.stroke-2"),sQuery(id+"F1.wireOp",EDGE,"E2.sketch_text.stroke-3"),sQuery(id+"F1.wireOp",EDGE,"E2.sketch_text.stroke-4"),sQuery(id+"F1.wireOp",EDGE,"E2.sketch_text.stroke-5"),sQuery(id+"F1.wireOp",EDGE,"E2.sketch_text.stroke-6"),sQuery(id+"F1.wireOp",EDGE,"E2.sketch_text.stroke-7"),sQuery(id+"F1.wireOp",EDGE,"E2.sketch_text.stroke-8"),sQuery(id+"F1.wireOp",EDGE,"E2.sketch_text.stroke-9"),sQuery(id+"F1.wireOp",EDGE,"E2.sketch_text.stroke-10"),sQuery(id+"F1.wireOp",EDGE,"E2.sketch_text.stroke-11"),sQuery(id+"F1.wireOp",EDGE,"E2.sketch_text.stroke-12"),sQuery(id+"F1.wireOp",EDGE,"E2.sketch_text.stroke-13"),sQuery(id+"F1.wireOp",EDGE,"E2.sketch_text.stroke-14"),sQuery(id+"F1.wireOp",EDGE,"E2.sketch_text.stroke-15"),sQuery(id+"F1.wireOp",EDGE,"E2.sketch_text.stroke-16"),sQuery(id+"F1.wireOp",EDGE,"E2.sketch_text.stroke-17"),sQuery(id+"F1.wireOp",EDGE,"E2.sketch_text.stroke-18")])],"isStart":false}),makeQuery(id+"F2.opExtrude","CAP_FACE",FACE,{"disambiguationData":[OSD([sQuery(id+"F1.wireOp",EDGE,"E2.sketch_text.stroke-19"),sQuery(id+"F1.wireOp",EDGE,"E2.sketch_text.stroke-20"),sQuery(id+"F1.wireOp",EDGE,"E2.sketch_text.stroke-21"),sQuery(id+"F1.wireOp",EDGE,"E2.sketch_text.stroke-22"),sQuery(id+"F1.wireOp",EDGE,"E2.sketch_text.stroke-23"),sQuery(id+"F1.wireOp",EDGE,"E2.sketch_text.stroke-24"),sQuery(id+"F1.wireOp",EDGE,"E2.sketch_text.stroke-25"),sQuery(id+"F1.wireOp",EDGE,"E2.sketch_text.stroke-26"),sQuery(id+"F1.wireOp",EDGE,"E2.sketch_text.stroke-27"),sQuery(id+"F1.wireOp",EDGE,"E2.sketch_text.stroke-28"),sQuery(id+"F1.wireOp",EDGE,"E2.sketch_text.stroke-29"),sQuery(id+"F1.wireOp",EDGE,"E2.sketch_text.stroke-30"),sQuery(id+"F1.wireOp",EDGE,"E2.sketch_text.stroke-31"),sQuery(id+"F1.wireOp",EDGE,"E2.sketch_text.stroke-32"),sQuery(id+"F1.wireOp",EDGE,"E2.sketch_text.stroke-33"),sQuery(id+"F1.wireOp",EDGE,"E2.sketch_text.stroke-34"),sQuery(id+"F1.wireOp",EDGE,"E2.sketch_text.stroke-35"),sQuery(id+"F1.wireOp",EDGE,"E2.sketch_text.stroke-36"),sQuery(id+"F1.wireOp",EDGE,"E2.sketch_text.stroke-37"),sQuery(id+"F1.wireOp",EDGE,"E2.sketch_text.stroke-38"),sQuery(id+"F1.wireOp",EDGE,"E2.sketch_text.stroke-39"),sQuery(id+"F1.wireOp",EDGE,"E2.sketch_text.stroke-40"),sQuery(id+"F1.wireOp",EDGE,"E2.sketch_text.stroke-41"),sQuery(id+"F1.wireOp",EDGE,"E2.sketch_text.stroke-42"),sQuery(id+"F1.wireOp",EDGE,"E2.sketch_text.stroke-43")])],"isStart":false}),makeQuery(id+"F2.opExtrude","CAP_FACE",FACE,{"disambiguationData":[OSD([sQuery(id+"F1.wireOp",EDGE,"E2.sketch_text.stroke-44"),sQuery(id+"F1.wireOp",EDGE,"E2.sketch_text.stroke-45"),sQuery(id+"F1.wireOp",EDGE,"E2.sketch_text.stroke-46"),sQuery(id+"F1.wireOp",EDGE,"E2.sketch_text.stroke-47"),sQuery(id+"F1.wireOp",EDGE,"E2.sketch_text.stroke-48"),sQuery(id+"F1.wireOp",EDGE,"E2.sketch_text.stroke-49"),sQuery(id+"F1.wireOp",EDGE,"E2.sketch_text.stroke-50"),sQuery(id+"F1.wireOp",EDGE,"E2.sketch_text.stroke-51"),sQuery(id+"F1.wireOp",EDGE,"E2.sketch_text.stroke-52"),sQuery(id+"F1.wireOp",EDGE,"E2.sketch_text.stroke-53"),sQuery(id+"F1.wireOp",EDGE,"E2.sketch_text.stroke-54"),sQuery(id+"F1.wireOp",EDGE,"E2.sketch_text.stroke-55"),sQuery(id+"F1.wireOp",EDGE,"E2.sketch_text.stroke-56"),sQuery(id+"F1.wireOp",EDGE,"E2.sketch_text.stroke-57"),sQuery(id+"F1.wireOp",EDGE,"E2.sketch_text.stroke-58"),sQuery(id+"F1.wireOp",EDGE,"E2.sketch_text.stroke-59"),sQuery(id+"F1.wireOp",EDGE,"E2.sketch_text.stroke-60")])],"isStart":false}),makeQuery(id+"F2.opExtrude","CAP_FACE",FACE,{"disambiguationData":[OSD([sQuery(id+"F1.wireOp",EDGE,"E2.sketch_text.stroke-61"),sQuery(id+"F1.wireOp",EDGE,"E2.sketch_text.stroke-62"),sQuery(id+"F1.wireOp",EDGE,"E2.sketch_text.stroke-63"),sQuery(id+"F1.wireOp",EDGE,"E2.sketch_text.stroke-64"),sQuery(id+"F1.wireOp",EDGE,"E2.sketch_text.stroke-65"),sQuery(id+"F1.wireOp",EDGE,"E2.sketch_text.stroke-66"),sQuery(id+"F1.wireOp",EDGE,"E2.sketch_text.stroke-67"),sQuery(id+"F1.wireOp",EDGE,"E2.sketch_text.stroke-68"),sQuery(id+"F1.wireOp",EDGE,"E2.sketch_text.stroke-69"),sQuery(id+"F1.wireOp",EDGE,"E2.sketch_text.stroke-70"),sQuery(id+"F1.wireOp",EDGE,"E2.sketch_text.stroke-71"),sQuery(id+"F1.wireOp",EDGE,"E2.sketch_text.stroke-72"),sQuery(id+"F1.wireOp",EDGE,"E2.sketch_text.stroke-73"),sQuery(id+"F1.wireOp",EDGE,"E2.sketch_text.stroke-74"),sQuery(id+"F1.wireOp",EDGE,"E2.sketch_text.stroke-75"),sQuery(id+"F1.wireOp",EDGE,"E2.sketch_text.stroke-76"),sQuery(id+"F1.wireOp",EDGE,"E2.sketch_text.stroke-77")])],"isStart":false}),makeQuery(id+"F2.opExtrude","CAP_FACE",FACE,{"disambiguationData":[OSD([sQuery(id+"F1.wireOp",EDGE,"E2.sketch_text.stroke-78"),sQuery(id+"F1.wireOp",EDGE,"E2.sketch_text.stroke-79"),sQuery(id+"F1.wireOp",EDGE,"E2.sketch_text.stroke-80"),sQuery(id+"F1.wireOp",EDGE,"E2.sketch_text.stroke-81"),sQuery(id+"F1.wireOp",EDGE,"E2.sketch_text.stroke-82"),sQuery(id+"F1.wireOp",EDGE,"E2.sketch_text.stroke-83"),sQuery(id+"F1.wireOp",EDGE,"E2.sketch_text.stroke-84"),sQuery(id+"F1.wireOp",EDGE,"E2.sketch_text.stroke-85"),sQuery(id+"F1.wireOp",EDGE,"E2.sketch_text.stroke-86"),sQuery(id+"F1.wireOp",EDGE,"E2.sketch_text.stroke-87"),sQuery(id+"F1.wireOp",EDGE,"E2.sketch_text.stroke-88"),sQuery(id+"F1.wireOp",EDGE,"E2.sketch_text.stroke-89"),sQuery(id+"F1.wireOp",EDGE,"E2.sketch_text.stroke-90"),sQuery(id+"F1.wireOp",EDGE,"E2.sketch_text.stroke-91"),sQuery(id+"F1.wireOp",EDGE,"E2.sketch_text.stroke-92"),sQuery(id+"F1.wireOp",EDGE,"E2.sketch_text.stroke-93"),sQuery(id+"F1.wireOp",EDGE,"E2.sketch_text.stroke-94"),sQuery(id+"F1.wireOp",EDGE,"E2.sketch_text.stroke-95")])],"isStart":false}),makeQuery(id+"F2.opExtrude","CAP_FACE",FACE,{"disambiguationData":[OSD([sQuery(id+"F1.wireOp",EDGE,"E2.sketch_text.stroke-96"),sQuery(id+"F1.wireOp",EDGE,"E2.sketch_text.stroke-97"),sQuery(id+"F1.wireOp",EDGE,"E2.sketch_text.stroke-98"),sQuery(id+"F1.wireOp",EDGE,"E2.sketch_text.stroke-99"),sQuery(id+"F1.wireOp",EDGE,"E2.sketch_text.stroke-100"),sQuery(id+"F1.wireOp",EDGE,"E2.sketch_text.stroke-101"),sQuery(id+"F1.wireOp",EDGE,"E2.sketch_text.stroke-102"),sQuery(id+"F1.wireOp",EDGE,"E2.sketch_text.stroke-103"),sQuery(id+"F1.wireOp",EDGE,"E2.sketch_text.stroke-104"),sQuery(id+"F1.wireOp",EDGE,"E2.sketch_text.stroke-105"),sQuery(id+"F1.wireOp",EDGE,"E2.sketch_text.stroke-106"),sQuery(id+"F1.wireOp",EDGE,"E2.sketch_text.stroke-107"),sQuery(id+"F1.wireOp",EDGE,"E2.sketch_text.stroke-108"),sQuery(id+"F1.wireOp",EDGE,"E2.sketch_text.stroke-109"),sQuery(id+"F1.wireOp",EDGE,"E2.sketch_text.stroke-110"),sQuery(id+"F1.wireOp",EDGE,"E2.sketch_text.stroke-111"),sQuery(id+"F1.wireOp",EDGE,"E2.sketch_text.stroke-112")])],"isStart":false})]})});
            extrude(context, id + "F7", {"entities" : qUnion([Q0, Q1, Q2, Q3, Q4, Q5, Q6, Q7]), "operationType" : NewBodyOperationType.REMOVE, "oppositeDirection" : true, "depth" : 25 * mm, "offsetDistance" : 25 * mm});
        }
    });
